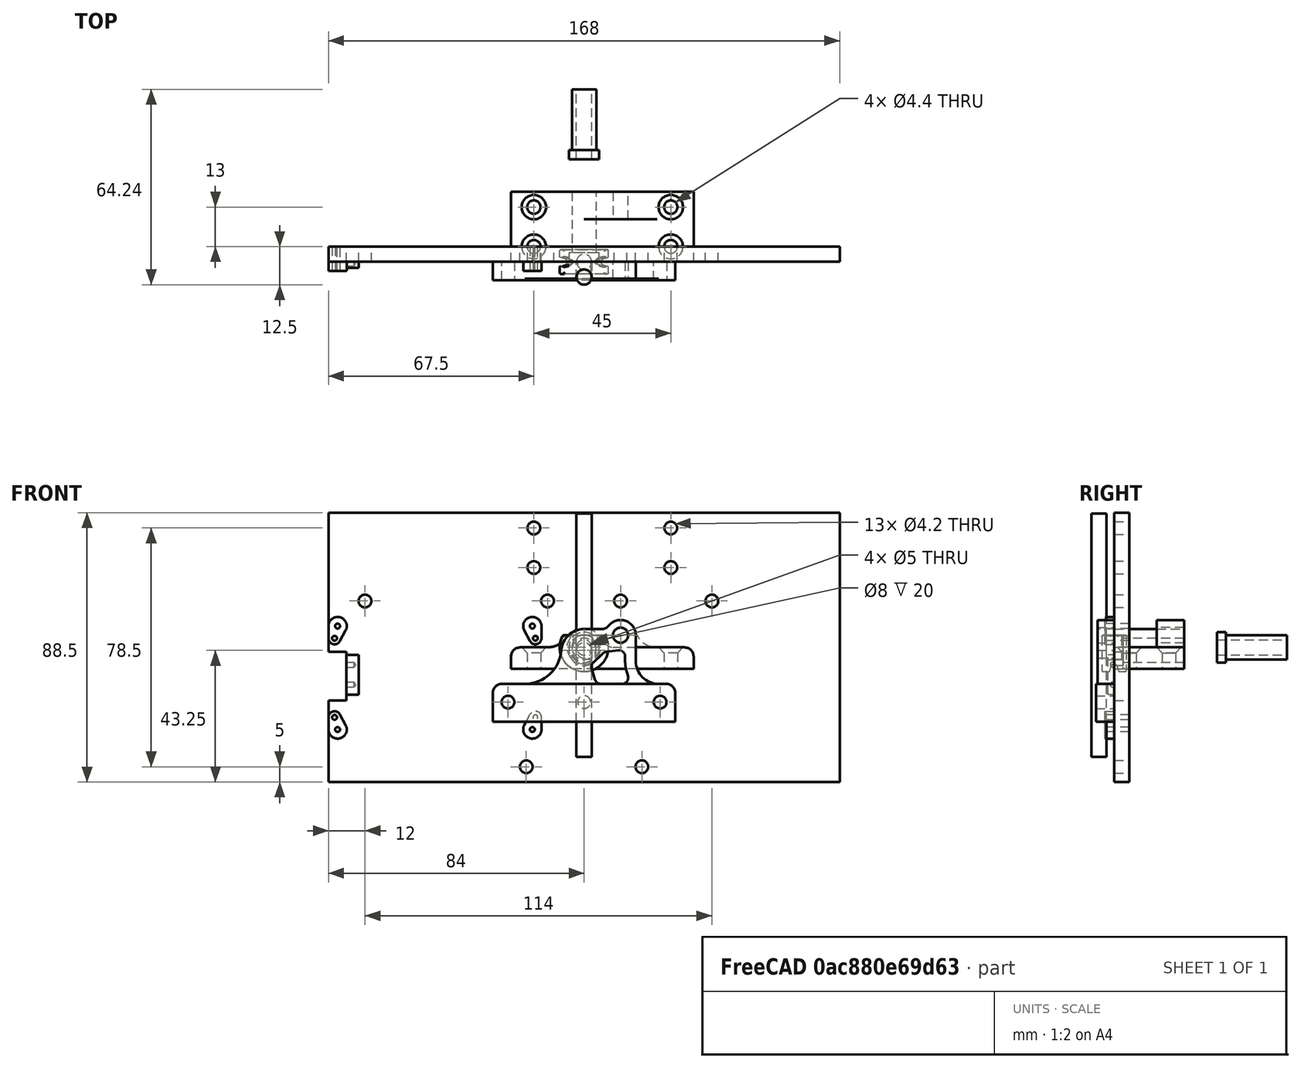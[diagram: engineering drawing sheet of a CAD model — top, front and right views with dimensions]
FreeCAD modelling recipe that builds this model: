
FCSTD DOCUMENT  (FreeCAD 0.18R14555 (Git shallow))
Label: door
License: All rights reserved
LicenseURL: http://en.wikipedia.org/wiki/All_rights_reserved
objects: Sketcher::SketchObject×18, TechDraw::DrawViewDimension×18, PartDesign::Pocket×7, PartDesign::Body×6, TechDraw::DrawProjGroupItem×5, PartDesign::Pad×4, PartDesign::Revolution×3, PartDesign::Hole×3, TechDraw::DrawSVGTemplate×3, TechDraw::DrawViewAnnotation×3, TechDraw::DrawProjGroup×3, TechDraw::DrawPage×3, PartDesign::Plane×2, PartDesign::Fillet×2, TechDraw::DrawViewSymbol×2, TechDraw::DrawViewPart×2, PartDesign::Line×1, TechDraw::DrawViewSection×1
note: 63 computed .brp shape members not serialized (recipe doc carries the construction recipe); baked Part::Feature solids carry a one-line shape summary decoded from their .brp

FEATURE [Sketcher::SketchObject] Sketch  label="Base"
  MapMode = 5
  Placement = pos=(0,0,0) rot=(1,0,0;1.5708rad)
  Support = -> [XZ_Plane]
  sketch-geometry (34):
    g0: LineSegment StartX=-84 StartY=44.25 StartZ=0 EndX=84 EndY=44.25 EndZ=0
    g1: LineSegment StartX=84 StartY=44.25 StartZ=0 EndX=84 EndY=-44.25 EndZ=0
    g2: LineSegment StartX=84 StartY=-44.25 StartZ=0 EndX=-84 EndY=-44.25 EndZ=0
    g3: LineSegment StartX=-84 StartY=-44.25 StartZ=0 EndX=-84 EndY=44.25 EndZ=0
    g4: LineSegment StartX=-4 StartY=43.25 StartZ=0 EndX=4 EndY=43.25 EndZ=0
    g5: LineSegment StartX=4 StartY=43.25 StartZ=0 EndX=4 EndY=37.25 EndZ=0
    g6: LineSegment StartX=-4 StartY=37.25 StartZ=0 EndX=-4 EndY=43.25 EndZ=0
    g7: LineSegment StartX=-2.5 StartY=54.25 StartZ=0 EndX=2.5 EndY=54.25 EndZ=0
    g8: LineSegment StartX=2.5 StartY=54.25 StartZ=0 EndX=2.5 EndY=-21.75 EndZ=0
    g9: LineSegment StartX=-4 StartY=-21.75 StartZ=0 EndX=-2.5 EndY=-21.75 EndZ=0
    g10: LineSegment StartX=4 StartY=-21.75 StartZ=0 EndX=4 EndY=-25.75 EndZ=0
    g11: LineSegment StartX=-4 StartY=-25.75 StartZ=0 EndX=-4 EndY=-21.75 EndZ=0
    g12: LineSegment StartX=-2.5 StartY=-21.75 StartZ=0 EndX=-2.5 EndY=54.25 EndZ=0
    g13: LineSegment StartX=2.5 StartY=-21.75 StartZ=0 EndX=4 EndY=-21.75 EndZ=0
    g14: LineSegment StartX=-4 StartY=-25.75 StartZ=0 EndX=4 EndY=-25.75 EndZ=0
    g15: LineSegment [constr] StartX=-40 StartY=30.25 StartZ=0 EndX=-7.5 EndY=30.25 EndZ=0
    g16: ArcOfCircle [constr] CenterX=-7.5 CenterY=27.25 CenterZ=0 NormalX=0 NormalY=0 NormalZ=1 AngleXU=0 Radius=3 StartAngle=0 EndAngle=1.5708
    g17: LineSegment [constr] StartX=-4.5 StartY=27.25 StartZ=0 EndX=-4.5 EndY=-23.75 EndZ=0
    g18: LineSegment [constr] StartX=-4.5 StartY=-23.75 StartZ=0 EndX=4.5 EndY=-23.75 EndZ=0
    g19: LineSegment [constr] StartX=4.5 StartY=-23.75 StartZ=0 EndX=4.5 EndY=27.25 EndZ=0
    g20: ArcOfCircle [constr] CenterX=7.5 CenterY=27.25 CenterZ=0 NormalX=0 NormalY=0 NormalZ=1 AngleXU=0 Radius=3 StartAngle=1.5708 EndAngle=3.14159
    g21: LineSegment [constr] StartX=7.5 StartY=30.25 StartZ=0 EndX=40 EndY=30.25 EndZ=0
    g22: LineSegment StartX=-4 StartY=51.25 StartZ=0 EndX=4 EndY=51.25 EndZ=0
    g23: LineSegment StartX=4 StartY=51.25 StartZ=0 EndX=4 EndY=45.25 EndZ=0
    g24: LineSegment StartX=4 StartY=45.25 StartZ=0 EndX=-4 EndY=45.25 EndZ=0
    g25: LineSegment StartX=-4 StartY=45.25 StartZ=0 EndX=-4 EndY=51.25 EndZ=0
    g26: Circle [constr] CenterX=7.5 CenterY=27.25 CenterZ=0 NormalX=0 NormalY=0 NormalZ=1 AngleXU=0 Radius=3
    g27: Circle [constr] CenterX=-7.5 CenterY=27.25 CenterZ=0 NormalX=0 NormalY=0 NormalZ=1 AngleXU=0 Radius=3
    g28: LineSegment StartX=5 StartY=37.25 StartZ=0 EndX=5 EndY=34.25 EndZ=0
    g29: LineSegment StartX=5 StartY=34.25 StartZ=0 EndX=-5 EndY=34.25 EndZ=0
    g30: LineSegment StartX=-5 StartY=34.25 StartZ=0 EndX=-5 EndY=37.25 EndZ=0
    g31: LineSegment StartX=5 StartY=37.25 StartZ=0 EndX=4 EndY=37.25 EndZ=0
    g32: LineSegment [constr] StartX=4 StartY=37.25 StartZ=0 EndX=-4 EndY=37.25 EndZ=0
    g33: LineSegment StartX=-5 StartY=37.25 StartZ=0 EndX=-4 EndY=37.25 EndZ=0
  constraints (89):
    c: Coincident(g0,g1)
    c: Coincident(g1,g2)
    c: Coincident(g2,g3)
    c: Coincident(g3,g0)
    c: Horizontal(g2)
    c: Vertical(g3)
    c: DistanceY(g1,g1) = 88.5  'doorHeight'
    c: DistanceX(g0,g0) = 168  'doorWidth'
    c: Symmetric(g0,g1,g-1)
    c: Symmetric(g0,g0,g-2)
    c: Coincident(g4,g5)
    c: Coincident(g6,g4)
    c: Vertical(g5)
    c: Vertical(g6)
    c: Symmetric(g4,g4,g-2)
    c: DistanceY(g4,g0) = 1
    c: DistanceY(g5,g5) = 6  'bushingLength'
    c: DistanceX(g4,g4) = 8
    c: Coincident(g7,g8)
    c: Coincident(g12,g7)
    c: Vertical(g8)
    c: Symmetric(g7,g7,g-2)
    c: DistanceX(g7,g7) = 5  'shaftOD'
    c: Coincident(g13,g10)
    c: Coincident(g11,g9)
    c: Horizontal(g9)
    c: Vertical(g10)
    c: Coincident(g9,g12)
    c: Coincident(g13,g8)
    c: Tangent(g9,g13)
    c: Equal(g13,g9)
    c: Equal(g10,g11)
    c: DistanceX(g9,g10) = 8  'springNotchOD'
    c: Coincident(g14,g11)
    c: Coincident(g14,g10)
    c: Vertical(g12)
    c: DistanceY(g11,g11) = 4  'springNotchHeight'
    c: DistanceY(g11,g7) = 80  'shaftLength'
    c: Horizontal(g15)
    c: Tangent(g15,g16) = 1.5708
    c: Tangent(g16,g17) = 1.5708
    c: Coincident(g17,g18)
    c: Coincident(g18,g19)
    c: Tangent(g19,g20) = 1.5708
    c: Tangent(g20,g21) = 1.5708
    c: PointOnObject(g15,g21)
    c: Horizontal(g21)
    c: Radius(g20) = 3  'rolerOD'
    c: Symmetric(g20,g16,g-2)
    c: Equal(g15,g21)
    c: Symmetric(g11,g9,g18)
    c: Coincident(g22,g23)
    c: Coincident(g23,g24)
    c: Coincident(g24,g25)
    c: Coincident(g25,g22)
    c: Horizontal(g24)
    c: Vertical(g23)
    c: Vertical(g25)
    c: Symmetric(g22,g22,g-2)
    c: Equal(g23,g5)
    c: Equal(g24,g4)
    c: Symmetric(g17,g18,g-2)
    c: DistanceX(g10,g18) = 0.5
    c: DistanceY(g0,g23) = 1
    c: DistanceX(g16,g20) = 15  'rolerDist'
    c: Coincident(g26,g20)
    c: PointOnObject(g20,g26)
    c: Coincident(g27,g16)
    c: PointOnObject(g15,g27)
    c: DistanceX(g15,g21) = 80
    c: DistanceY(g15,g0) = 14  'rolerHeight'
    c: DistanceY(g11,g0) = 70
    c: Coincident(g28,g29)
    c: Coincident(g29,g30)
    c: Horizontal(g29)
    c: Vertical(g28)
    c: Vertical(g30)
    c: Coincident(g31,g28)
    c: Horizontal(g31)
    c: Coincident(g31,g5)
    c: Coincident(g32,g5)
    c: Horizontal(g32)
    c: Coincident(g32,g6)
    c: Coincident(g33,g30)
    c: Horizontal(g33)
    c: Coincident(g33,g6)
    c: Equal(g33,g31)
    c: DistanceX(g29,g29) = 10
    c: DistanceY(g30,g30) = 3
FEATURE [Sketcher::SketchObject] Sketch001
  MapMode = 5
  Placement = pos=(0,0,0) rot=(1,0,0;1.5708rad)
  Support = -> [XZ_Plane]
  expr: Constraints[7] = Sketch.Constraints.doorWidth
  expr: Constraints[6] = Sketch.Constraints.doorHeight
  sketch-geometry (8):
    g0: LineSegment [constr] StartX=-84 StartY=44.25 StartZ=0 EndX=84 EndY=44.25 EndZ=0
    g1: LineSegment [constr] StartX=84 StartY=44.25 StartZ=0 EndX=84 EndY=-44.25 EndZ=0
    g2: LineSegment [constr] StartX=84 StartY=-44.25 StartZ=0 EndX=-84 EndY=-44.25 EndZ=0
    g3: LineSegment [constr] StartX=-84 StartY=-44.25 StartZ=0 EndX=-84 EndY=44.25 EndZ=0
    g4: LineSegment StartX=-84 StartY=44.25 StartZ=0 EndX=84 EndY=44.25 EndZ=0
    g5: LineSegment StartX=84 StartY=44.25 StartZ=0 EndX=84 EndY=-44.25 EndZ=0
    g6: LineSegment StartX=84 StartY=-44.25 StartZ=0 EndX=-84 EndY=-44.25 EndZ=0
    g7: LineSegment StartX=-84 StartY=-44.25 StartZ=0 EndX=-84 EndY=44.25 EndZ=0
  constraints (19):
    c: Coincident(g0,g1)
    c: Coincident(g1,g2)
    c: Coincident(g2,g3)
    c: Coincident(g3,g0)
    c: Horizontal(g2)
    c: Vertical(g3)
    c: DistanceY(g1,g1) = 88.5
    c: DistanceX(g0,g0) = 168
    c: Symmetric(g0,g1,g-1)
    c: Symmetric(g0,g0,g-2)
    c: Coincident(g4,g5)
    c: Coincident(g5,g6)
    c: Coincident(g6,g7)
    c: Coincident(g7,g4)
    c: Horizontal(g4)
    c: Vertical(g5)
    c: Coincident(g4,g0)
    c: Coincident(g6,g2)
    c: Coincident(g1,g5)
FEATURE [PartDesign::Pad] Pad
  Length = 5
  Length2 = 100
  Placement = pos=(0,0,0) rot=(1,0,0;1.5708rad)
  Profile = -> Sketch001
  Reversed = true
  Type = 0
FEATURE [Sketcher::SketchObject] Sketch013  label="BushingSketch"
  MapMode = 5
  Support = -> [XY_Plane003]
  sketch-geometry (6):
    g0: LineSegment StartX=2.5 StartY=56.7373 StartZ=0 EndX=4 EndY=56.7373 EndZ=0
    g1: LineSegment StartX=4 StartY=56.7373 StartZ=0 EndX=4 EndY=36.7373 EndZ=0
    g2: LineSegment StartX=4 StartY=36.7373 StartZ=0 EndX=5 EndY=36.7373 EndZ=0
    g3: LineSegment StartX=5 StartY=36.7373 StartZ=0 EndX=5 EndY=33.7373 EndZ=0
    g4: LineSegment StartX=5 StartY=33.7373 StartZ=0 EndX=2.5 EndY=33.7373 EndZ=0
    g5: LineSegment StartX=2.5 StartY=33.7373 StartZ=0 EndX=2.5 EndY=56.7373 EndZ=0
  constraints (17):
    c: Horizontal(g0)
    c: Coincident(g0,g1)
    c: Vertical(g1)
    c: Coincident(g1,g2)
    c: Horizontal(g2)
    c: Coincident(g2,g3)
    c: Vertical(g3)
    c: Coincident(g3,g4)
    c: Horizontal(g4)
    c: Coincident(g4,g5)
    c: Coincident(g5,g0)
    c: Vertical(g5)
    c: DistanceX(g-1,g0) = 4
    c: DistanceX(g-1,g3) = 5
    c: DistanceX(g-1,g4) = 2.5
    c: DistanceY(g3,g3) = 3
    c: DistanceY(g3,g0) = 23  'BushingHeight'
FEATURE [PartDesign::Revolution] Revolution001
  Angle = 360
  Axis = (0,1,0)
  Base = (0,0,0)
  Profile = -> Sketch013
  ReferenceAxis = -> Sketch013 [V_Axis]
  Reversed = true
FEATURE [PartDesign::Body] Body003  label="Bushing"
  Group = -> [Sketch013,Revolution001]
  Origin = -> Origin003
  Tip = -> Revolution001
FEATURE [Sketcher::SketchObject] Sketch014
  MapMode = 5
  Placement = pos=(0,0,0) rot=(0.57735,0.57735,0.57735;2.0944rad)
  Support = -> [YZ_Plane004]
  sketch-geometry (11):
    g0: LineSegment StartX=-4 StartY=0 StartZ=0 EndX=-4 EndY=-8 EndZ=0
    g1: LineSegment StartX=-4 StartY=-8 StartZ=0 EndX=-1.5 EndY=-8 EndZ=0
    g2: LineSegment StartX=-1.5 StartY=-8 StartZ=0 EndX=-0.956943 EndY=-6.20972 EndZ=0
    g3: ArcOfCircle CenterX=2e-16 CenterY=-6.5 CenterZ=0 NormalX=0 NormalY=0 NormalZ=1 AngleXU=0 Radius=1 StartAngle=0.294515 EndAngle=2.84708
    g4: LineSegment StartX=0.956943 StartY=-6.20972 StartZ=0 EndX=1.5 EndY=-8 EndZ=0
    g5: LineSegment StartX=1.5 StartY=-8 StartZ=0 EndX=4 EndY=-8 EndZ=0
    g6: LineSegment StartX=4 StartY=-8 StartZ=0 EndX=4 EndY=0 EndZ=0
    g7: LineSegment StartX=4 StartY=0 StartZ=0 EndX=-4 EndY=0 EndZ=0
    g8: LineSegment [constr] StartX=-1.5 StartY=-8 StartZ=0 EndX=2e-16 EndY=-8 EndZ=0
    g9: LineSegment [constr] StartX=2e-16 StartY=-8 StartZ=0 EndX=1.5 EndY=-8 EndZ=0
    g10: LineSegment [constr] StartX=2e-16 StartY=-8 StartZ=0 EndX=2e-16 EndY=-6.5 EndZ=0
  constraints (29):
    c: PointOnObject(g0,g-1)
    c: Vertical(g0)
    c: Coincident(g0,g1)
    c: Horizontal(g1)
    c: Coincident(g1,g2)
    c: Tangent(g2,g3) = 1.5708
    c: Tangent(g3,g4) = 1.5708
    c: Coincident(g4,g5)
    c: Horizontal(g5)
    c: Coincident(g5,g6)
    c: Vertical(g6)
    c: Coincident(g6,g7)
    c: Coincident(g7,g0)
    c: PointOnObject(g4,g1)
    c: Equal(g1,g5)
    c: Coincident(g8,g1)
    c: Horizontal(g8)
    c: Coincident(g9,g8)
    c: Coincident(g9,g4)
    c: Equal(g8,g9)
    c: Coincident(g10,g8)
    c: Vertical(g10)
    c: Coincident(g3,g10)
    c: DistanceY(g0,g0) = 8
    c: DistanceX(g7,g7) = 8
    c: DistanceX(g1,g4) = 3
    c: DistanceY(g10,g10) = 1.5
    c: Radius(g3) = 1
    c: Symmetric(g6,g0,g-2)
FEATURE [PartDesign::Revolution] Revolution002
  Angle = 360
  Axis = (1e-16,1,-1e-16)
  Base = (0,0,0)
  Placement = pos=(0,0,0) rot=(0.57735,0.57735,0.57735;2.0944rad)
  Profile = -> Sketch014
  ReferenceAxis = -> Y_Axis004
FEATURE [PartDesign::Plane] DatumPlane003
  AttachmentOffset = pos=(0,0,4) rot=(0,0,1;0rad)
  Length = 24
  MapMode = 5
  Placement = pos=(0,0,4) rot=(0,0,1;0rad)
  ResizeMode = 0
  Support = -> [XY_Plane004]
  Width = 24
FEATURE [Sketcher::SketchObject] Sketch015
  MapMode = 5
  Placement = pos=(0,0,0) rot=(1,0,0;1.5708rad)
  Support = -> [XZ_Plane004]
  sketch-geometry (4):
    g0: LineSegment StartX=-8 StartY=20 StartZ=0 EndX=8 EndY=20 EndZ=0
    g1: LineSegment StartX=8 StartY=20 StartZ=0 EndX=8 EndY=4 EndZ=0
    g2: LineSegment StartX=8 StartY=4 StartZ=0 EndX=-8 EndY=4 EndZ=0
    g3: LineSegment StartX=-8 StartY=4 StartZ=0 EndX=-8 EndY=20 EndZ=0
  constraints (11):
    c: Coincident(g0,g1)
    c: Coincident(g1,g2)
    c: Coincident(g2,g3)
    c: Coincident(g3,g0)
    c: Horizontal(g2)
    c: Vertical(g1)
    c: Vertical(g3)
    c: Symmetric(g0,g0,g-2)
    c: DistanceX(g0,g0) = 16
    c: Equal(g0,g1)
    c: DistanceY(g-1,g1) = 4
FEATURE [PartDesign::Pocket] Pocket
  BaseFeature = -> Revolution002
  Length = 5
  Length2 = 100
  Midplane = true
  Placement = pos=(0,0,0) rot=(0.57735,0.57735,0.57735;2.0944rad)
  Profile = -> Sketch015
  Type = 1
FEATURE [Sketcher::SketchObject] Sketch016
  MapMode = 5
  Placement = pos=(0,0,4) rot=(0,0,1;0rad)
  Support = -> [DatumPlane003]
  expr: Constraints[1] = <<Base>>.Constraints.shaftOD
  sketch-geometry (1):
    g0: Circle CenterX=0 CenterY=0 CenterZ=0 NormalX=0 NormalY=0 NormalZ=1 AngleXU=0 Radius=2.5
  constraints (2):
    c: Coincident(g0,g-1)
    c: Diameter(g0) = 5
FEATURE [PartDesign::Pocket] Pocket002
  BaseFeature = -> Pocket
  Length = 8
  Length2 = 100
  Placement = pos=(0,0,0) rot=(0.57735,0.57735,0.57735;2.0944rad)
  Profile = -> Sketch016
  Type = 0
FEATURE [PartDesign::Fillet] Fillet
  Base = -> Pocket002 [Edge3,Edge18,Edge25,Edge28]
  BaseFeature = -> Pocket002
  Placement = pos=(0,0,0) rot=(0.57735,0.57735,0.57735;2.0944rad)
  Radius = 0.4
FEATURE [PartDesign::Fillet] Fillet001
  Base = -> Fillet [Edge1]
  BaseFeature = -> Fillet
  Placement = pos=(0,0,0) rot=(0.57735,0.57735,0.57735;2.0944rad)
  Radius = 0.4
FEATURE [PartDesign::Body] Body004  label="Slider"
  Group = -> [Sketch014,Revolution002,DatumPlane003,Sketch015,Pocket,Sketch016,Pocket002,Fillet,Fillet001]
  Origin = -> Origin004
  Tip = -> Fillet001
FEATURE [PartDesign::Line] DatumLine
  AttacherType = Attacher::AttachEngineLine
  AttachmentOffset = pos=(0,5,0) rot=(0,0,1;0rad)
  MapMode = 17
  Placement = pos=(0,-5,-1.1e-15) rot=(1,0,0;3.14159rad)
  Support = -> [XZ_Plane001]
FEATURE [PartDesign::Plane] DatumPlane
  AttachmentOffset = pos=(0,0,5) rot=(0,0,1;0rad)
  Length = 28
  MapMode = 5
  Placement = pos=(0,-5,-1.1e-15) rot=(1,0,0;1.5708rad)
  ResizeMode = 0
  Support = -> [XZ_Plane001]
  Width = 88
FEATURE [Sketcher::SketchObject] Sketch004
  MapMode = 5
  Placement = pos=(0,-5,-1.1e-15) rot=(1,0,0;1.5708rad)
  Support = -> [DatumPlane]
  expr: Constraints[9] = Sketch.Constraints.shaftOD / 2
  expr: Constraints[8] = Sketch.Constraints.shaftLength
  sketch-geometry (4):
    g0: LineSegment StartX=0 StartY=-36.0556 StartZ=0 EndX=2.5 EndY=-36.0556 EndZ=0
    g1: LineSegment StartX=2.5 StartY=-36.0556 StartZ=0 EndX=2.5 EndY=43.9444 EndZ=0
    g2: LineSegment StartX=2.5 StartY=43.9444 StartZ=0 EndX=0 EndY=43.9444 EndZ=0
    g3: LineSegment StartX=0 StartY=43.9444 StartZ=0 EndX=0 EndY=-36.0556 EndZ=0
  constraints (11):
    c: Horizontal(g0)
    c: Vertical(g1)
    c: Coincident(g1,g2)
    c: Coincident(g2,g3)
    c: Vertical(g3)
    c: Coincident(g0,g3)
    c: Horizontal(g2)
    c: PointOnObject(g2,g-2)
    c: DistanceY(g3,g3) = 80
    c: DistanceX(g2,g2) = 2.5
    c: Coincident(g0,g1)
FEATURE [PartDesign::Revolution] Revolution
  Angle = 360
  Axis = (0,-2e-16,1)
  Base = (0,-5,-1.1e-15)
  Placement = pos=(0,-5,-1e-15) rot=(1,0,0;1.5708rad)
  Profile = -> Sketch004
  ReferenceAxis = -> Sketch004 [V_Axis]
  Reversed = true
FEATURE [PartDesign::Body] Body001  label="Pin"
  Group = -> [DatumLine,DatumPlane,Sketch004,Revolution]
  Origin = -> Origin001
  Tip = -> Revolution
FEATURE [Sketcher::SketchObject] Sketch018
  MapMode = 5
  Placement = pos=(0,0,0) rot=(1,0,0;1.5708rad)
  Support = -> [XZ_Plane]
  expr: Constraints[10] = <<Base>>.Constraints.doorWidth / 2mm
  sketch-geometry (46):
    g0: LineSegment [constr] StartX=-84 StartY=10 StartZ=0 EndX=-14 EndY=10 EndZ=0
    g1: LineSegment [constr] StartX=-14 StartY=10 StartZ=0 EndX=-14 EndY=-30 EndZ=0
    g2: LineSegment [constr] StartX=-14 StartY=-30 StartZ=0 EndX=-84 EndY=-30 EndZ=0
    g3: LineSegment [constr] StartX=-84 StartY=-30 StartZ=0 EndX=-84 EndY=10 EndZ=0
    g4: LineSegment [constr] StartX=-81 StartY=7 StartZ=0 EndX=-17 EndY=7 EndZ=0
    g5: LineSegment [constr] StartX=-17 StartY=7 StartZ=0 EndX=-17 EndY=-27 EndZ=0
    g6: LineSegment [constr] StartX=-17 StartY=-27 StartZ=0 EndX=-81 EndY=-27 EndZ=0
    g7: LineSegment [constr] StartX=-81 StartY=-27 StartZ=0 EndX=-81 EndY=7 EndZ=0
    g8: Circle [constr] CenterX=-81 CenterY=7 CenterZ=0 NormalX=0 NormalY=0 NormalZ=1 AngleXU=0 Radius=0.8
    g9: Circle [constr] CenterX=-17 CenterY=7 CenterZ=0 NormalX=0 NormalY=0 NormalZ=1 AngleXU=0 Radius=0.8
    g10: Circle [constr] CenterX=-17 CenterY=-27 CenterZ=0 NormalX=0 NormalY=0 NormalZ=1 AngleXU=0 Radius=0.8
    g11: Circle [constr] CenterX=-81 CenterY=-27 CenterZ=0 NormalX=0 NormalY=0 NormalZ=1 AngleXU=0 Radius=0.8
    g12: LineSegment [constr] StartX=-84 StartY=-2.5 StartZ=0 EndX=-78.1 EndY=-2.5 EndZ=0
    g13: LineSegment [constr] StartX=-78.1 StartY=-2.5 StartZ=0 EndX=-78.1 EndY=-15.5 EndZ=0
    g14: LineSegment [constr] StartX=-78.1 StartY=-15.5 StartZ=0 EndX=-84 EndY=-15.5 EndZ=0
    g15: LineSegment [constr] StartX=-84 StartY=-15.5 StartZ=0 EndX=-84 EndY=-2.5 EndZ=0
    g16: Circle [constr] CenterX=-17 CenterY=7 CenterZ=0 NormalX=0 NormalY=0 NormalZ=1 AngleXU=0 Radius=3
    g17: Circle [constr] CenterX=-81 CenterY=7 CenterZ=0 NormalX=0 NormalY=0 NormalZ=1 AngleXU=0 Radius=3
    g18: Circle [constr] CenterX=-81 CenterY=-27 CenterZ=0 NormalX=0 NormalY=0 NormalZ=1 AngleXU=0 Radius=3
    g19: Circle [constr] CenterX=-17 CenterY=-27 CenterZ=0 NormalX=0 NormalY=0 NormalZ=1 AngleXU=0 Radius=3
    g20: LineSegment StartX=-78.1 StartY=-2.5 StartZ=0 EndX=-74.1 EndY=-2.5 EndZ=0
    g21: LineSegment StartX=-74.1 StartY=-2.5 StartZ=0 EndX=-74.1 EndY=-15.5 EndZ=0
    g22: LineSegment StartX=-74.1 StartY=-15.5 StartZ=0 EndX=-78.1 EndY=-15.5 EndZ=0
    g23: LineSegment StartX=-78.1 StartY=-15.5 StartZ=0 EndX=-78.1 EndY=-2.5 EndZ=0
    g24: LineSegment [constr] StartX=-49 StartY=7 StartZ=0 EndX=-49 EndY=-27 EndZ=0
    g25: LineSegment [constr] StartX=-82 StartY=3 StartZ=0 EndX=-16 EndY=3 EndZ=0
    g26: LineSegment [constr] StartX=-16 StartY=3 StartZ=0 EndX=-16 EndY=-23 EndZ=0
    g27: LineSegment [constr] StartX=-16 StartY=-23 StartZ=0 EndX=-82 EndY=-23 EndZ=0
    g28: LineSegment [constr] StartX=-82 StartY=-23 StartZ=0 EndX=-82 EndY=3 EndZ=0
    g29: LineSegment [constr] StartX=-17 StartY=-10 StartZ=0 EndX=-81 EndY=-10 EndZ=0
    g30: ArcOfCircle CenterX=-17 CenterY=7 CenterZ=0 NormalX=0 NormalY=0 NormalZ=1 AngleXU=0 Radius=3 StartAngle=2e-16 EndAngle=3.63155
    g31: ArcOfCircle CenterX=-16 CenterY=3 CenterZ=0 NormalX=0 NormalY=0 NormalZ=1 AngleXU=0 Radius=2 StartAngle=3.63155 EndAngle=6.28319
    g32: LineSegment StartX=-19.6471 StartY=5.58824 StartZ=0 EndX=-17.7647 EndY=2.05882 EndZ=0
    g33: LineSegment StartX=-14 StartY=7 StartZ=0 EndX=-14 EndY=3 EndZ=0
    g34: ArcOfCircle CenterX=-17 CenterY=-27 CenterZ=0 NormalX=0 NormalY=0 NormalZ=1 AngleXU=0 Radius=3 StartAngle=2.65164 EndAngle=6.28319
    g35: ArcOfCircle CenterX=-16 CenterY=-23 CenterZ=0 NormalX=0 NormalY=0 NormalZ=1 AngleXU=0 Radius=2 StartAngle=1e-16 EndAngle=2.65164
    g36: LineSegment StartX=-14 StartY=-27 StartZ=0 EndX=-14 EndY=-23 EndZ=0
    g37: LineSegment StartX=-19.6471 StartY=-25.5882 StartZ=0 EndX=-17.7647 EndY=-22.0588 EndZ=0
    g38: ArcOfCircle CenterX=-82 CenterY=-23 CenterZ=0 NormalX=0 NormalY=0 NormalZ=1 AngleXU=0 Radius=2 StartAngle=0.489957 EndAngle=3.14159
    g39: ArcOfCircle CenterX=-81 CenterY=-27 CenterZ=0 NormalX=0 NormalY=0 NormalZ=1 AngleXU=0 Radius=3 StartAngle=3.14159 EndAngle=6.77314
    g40: LineSegment StartX=-84 StartY=-23 StartZ=0 EndX=-84 EndY=-27 EndZ=0
    g41: LineSegment StartX=-80.2353 StartY=-22.0588 StartZ=0 EndX=-78.3529 EndY=-25.5882 EndZ=0
    g42: ArcOfCircle CenterX=-81 CenterY=7 CenterZ=0 NormalX=0 NormalY=0 NormalZ=1 AngleXU=0 Radius=3 StartAngle=5.79323 EndAngle=9.42478
    g43: ArcOfCircle CenterX=-82 CenterY=3 CenterZ=0 NormalX=0 NormalY=0 NormalZ=1 AngleXU=0 Radius=2 StartAngle=3.14159 EndAngle=5.79323
    g44: LineSegment StartX=-84 StartY=7 StartZ=0 EndX=-84 EndY=3 EndZ=0
    g45: LineSegment StartX=-78.3529 StartY=5.58824 StartZ=0 EndX=-80.2353 EndY=2.05882 EndZ=0
  constraints (110):
    c: Coincident(g0,g1)
    c: Coincident(g1,g2)
    c: Coincident(g2,g3)
    c: Coincident(g3,g0)
    c: Horizontal(g0)
    c: Horizontal(g2)
    c: Vertical(g1)
    c: Vertical(g3)
    c: DistanceX(g2,g2) = 70
    c: DistanceY(g1,g1) = 40
    c: DistanceX(g0,g-1) = 84
    c: DistanceY(g-1,g0) = 10
    c: Coincident(g4,g5)
    c: Coincident(g5,g6)
    c: Coincident(g6,g7)
    c: Coincident(g7,g4)
    c: Horizontal(g4)
    c: Horizontal(g6)
    c: Vertical(g5)
    c: Vertical(g7)
    c: DistanceX(g4,g0) = 3
    c: DistanceY(g4,g0) = 3
    c: DistanceX(g0,g4) = 3
    c: DistanceY(g2,g6) = 3
    c: Coincident(g8,g4)
    c: Coincident(g9,g4)
    c: Coincident(g10,g5)
    c: Coincident(g11,g6)
    c: Diameter(g11) = 1.6
    c: Equal(g11,g8)
    c: Equal(g11,g9)
    c: Equal(g11,g10)
    c: Coincident(g12,g13)
    c: Coincident(g13,g14)
    c: Coincident(g14,g15)
    c: Coincident(g15,g12)
    c: Horizontal(g12)
    c: Horizontal(g14)
    c: Vertical(g13)
    c: Vertical(g15)
    c: PointOnObject(g12,g3)
    c: DistanceX(g14,g13) = 5.9
    c: DistanceY(g2,g13) = 14.5
    c: DistanceY(g13,g13) = 13
    c: Coincident(g16,g4)
    c: Coincident(g17,g4)
    c: Coincident(g18,g6)
    c: Coincident(g19,g5)
    c: Coincident(g20,g21)
    c: Coincident(g21,g22)
    c: Coincident(g22,g23)
    c: Coincident(g23,g20)
    c: Horizontal(g20)
    c: Horizontal(g22)
    c: Vertical(g21)
    c: Coincident(g20,g12)
    c: Coincident(g22,g13)
    c: DistanceX(g20,g20) = 4
    c: Diameter(g17) = 6
    c: Equal(g17,g16)
    c: Equal(g17,g19)
    c: Equal(g17,g18)
    c: PointOnObject(g24,g4)
    c: PointOnObject(g24,g6)
    c: Symmetric(g17,g16,g24)
    c: Coincident(g25,g26)
    c: Coincident(g26,g27)
    c: Coincident(g27,g28)
    c: Coincident(g28,g25)
    c: Horizontal(g27)
    c: Vertical(g28)
    c: Symmetric(g25,g25,g24)
    c: DistanceX(g25,g25) = 66
    c: PointOnObject(g29,g5)
    c: PointOnObject(g29,g7)
    c: Symmetric(g19,g16,g29)
    c: Symmetric(g26,g25,g29)
    c: DistanceY(g26,g26) = 26
    c: Tangent(g30,g33) = 1.5708
    c: Tangent(g30,g32) = -1.5708
    c: Tangent(g32,g31) = -1.5708
    c: Tangent(g33,g31) = 1.5708
    c: Coincident(g30,g16)
    c: Equal(g30,g16)
    c: Coincident(g31,g25)
    c: Vertical(g33)
    c: Tangent(g34,g37) = 1.5708
    c: Tangent(g34,g36) = -1.5708
    c: Tangent(g36,g35) = -1.5708
    c: Tangent(g37,g35) = 1.5708
    c: Vertical(g36)
    c: Coincident(g34,g5)
    c: Equal(g34,g19)
    c: Coincident(g35,g26)
    c: Tangent(g38,g41) = 1.5708
    c: Tangent(g38,g40) = -1.5708
    c: Tangent(g40,g39) = -1.5708
    c: Tangent(g41,g39) = 1.5708
    c: Vertical(g40)
    c: Coincident(g38,g27)
    c: Coincident(g39,g6)
    c: Equal(g39,g18)
    c: Tangent(g42,g45) = 1.5708
    c: Tangent(g42,g44) = -1.5708
    c: Tangent(g44,g43) = -1.5708
    c: Tangent(g45,g43) = 1.5708
    c: Vertical(g44)
    c: Coincident(g42,g17)
    c: Equal(g42,g17)
    c: Coincident(g43,g25)
FEATURE [Sketcher::SketchObject] Sketch020  label="lockSketch"
  MapMode = 5
  Placement = pos=(0,0,0) rot=(1,0,0;1.5708rad)
  Support = -> [XZ_Plane007]
  sketch-geometry (35):
    g0: Circle CenterX=0 CenterY=-1 CenterZ=0 NormalX=0 NormalY=0 NormalZ=1 AngleXU=0 Radius=2.5
    g1: LineSegment StartX=30 StartY=-24.5 StartZ=0 EndX=-30 EndY=-24.5 EndZ=0
    g2: LineSegment [constr] StartX=25 StartY=-18 StartZ=0 EndX=0 EndY=-18 EndZ=0
    g3: LineSegment [constr] StartX=0 StartY=-18 StartZ=0 EndX=-25 EndY=-18 EndZ=0
    g4: Circle CenterX=-25 CenterY=-18 CenterZ=0 NormalX=0 NormalY=0 NormalZ=1 AngleXU=0 Radius=2.1
    g5: Circle CenterX=0 CenterY=-18 CenterZ=0 NormalX=0 NormalY=0 NormalZ=1 AngleXU=0 Radius=2.1
    g6: Circle CenterX=25 CenterY=-18 CenterZ=0 NormalX=0 NormalY=0 NormalZ=1 AngleXU=0 Radius=2.1
    g7: LineSegment StartX=-27 StartY=-12 StartZ=0 EndX=-19.4422 EndY=-12 EndZ=0
    g8: Circle CenterX=12 CenterY=4 CenterZ=0 NormalX=0 NormalY=0 NormalZ=1 AngleXU=0 Radius=2.5
    g9: LineSegment StartX=-30 StartY=-24.5 StartZ=0 EndX=-30 EndY=-15 EndZ=0
    g10: ArcOfCircle CenterX=-27 CenterY=-15 CenterZ=0 NormalX=0 NormalY=0 NormalZ=1 AngleXU=0 Radius=3 StartAngle=1.5708 EndAngle=3.14159
    g11: LineSegment StartX=30 StartY=-24.5 StartZ=0 EndX=30 EndY=-15 EndZ=0
    g12: ArcOfCircle CenterX=27 CenterY=-15 CenterZ=0 NormalX=0 NormalY=0 NormalZ=1 AngleXU=0 Radius=3 StartAngle=0 EndAngle=1.5708
    g13: LineSegment StartX=27 StartY=-12 StartZ=0 EndX=24.5 EndY=-12 EndZ=0
    g14: ArcOfCircle CenterX=24.5 CenterY=-4.5 CenterZ=0 NormalX=0 NormalY=0 NormalZ=1 AngleXU=0 Radius=7.5 StartAngle=3.14159 EndAngle=4.71239
    g15: LineSegment StartX=17 StartY=-4.5 StartZ=0 EndX=17 EndY=4 EndZ=0
    g16: ArcOfCircle CenterX=12 CenterY=4 CenterZ=0 NormalX=0 NormalY=0 NormalZ=1 AngleXU=0 Radius=5 StartAngle=0 EndAngle=2.46646
    g17: ArcOfCircle CenterX=5.755 CenterY=9 CenterZ=0 NormalX=0 NormalY=0 NormalZ=1 AngleXU=0 Radius=3 StartAngle=4.71239 EndAngle=5.60805
    g18: LineSegment StartX=5.755 StartY=6 StartZ=0 EndX=9e-16 EndY=6 EndZ=0
    g19: ArcOfCircle CenterX=0 CenterY=-1.5 CenterZ=0 NormalX=0 NormalY=0 NormalZ=1 AngleXU=0 Radius=7.5 StartAngle=1.5708 EndAngle=3.06459
    g20: ArcOfCircle CenterX=-19.4422 CenterY=2e-16 CenterZ=0 NormalX=0 NormalY=0 NormalZ=1 AngleXU=0 Radius=12 StartAngle=4.71239 EndAngle=6.20619
    g21: Circle [constr] CenterX=0 CenterY=-1 CenterZ=0 NormalX=0 NormalY=0 NormalZ=1 AngleXU=0 Radius=5
    g22: Circle [constr] CenterX=12 CenterY=4 CenterZ=0 NormalX=0 NormalY=0 NormalZ=1 AngleXU=0 Radius=5
    g23: LineSegment StartX=12.5 StartY=-12 StartZ=0 EndX=5.5 EndY=-12 EndZ=0
    g24: LineSegment StartX=3.5847 StartY=-10.5759 StartZ=0 EndX=2.50952 EndY=-7 EndZ=0
    g25: LineSegment StartX=3.04281 StartY=-4.97841 StartZ=0 EndX=6.11799 EndY=-2.03871 EndZ=0
    g26: LineSegment StartX=7.25081 StartY=-1.5 StartZ=0 EndX=11.2508 EndY=-0.997705 EndZ=0
    g27: LineSegment StartX=13.5 StartY=-2.98212 StartZ=0 EndX=13.5 EndY=-4.5 EndZ=0
    g28: LineSegment StartX=13.8565 StartY=-7.27791 StartZ=0 EndX=14.4352 EndY=-9.49493 EndZ=0
    g29: ArcOfCircle CenterX=12.5 CenterY=-10 CenterZ=0 NormalX=0 NormalY=0 NormalZ=1 AngleXU=0 Radius=2 StartAngle=4.71239 EndAngle=6.53849
    g30: ArcOfCircle CenterX=5.5 CenterY=-10 CenterZ=0 NormalX=0 NormalY=0 NormalZ=1 AngleXU=0 Radius=2 StartAngle=3.43367 EndAngle=4.71239
    g31: ArcOfCircle CenterX=4.42481 CenterY=-6.42411 CenterZ=0 NormalX=0 NormalY=0 NormalZ=1 AngleXU=0 Radius=2 StartAngle=2.33367 EndAngle=3.43367
    g32: ArcOfCircle CenterX=7.5 CenterY=-3.48442 CenterZ=0 NormalX=0 NormalY=0 NormalZ=1 AngleXU=0 Radius=2 StartAngle=1.69572 EndAngle=2.33367
    g33: ArcOfCircle CenterX=11.5 CenterY=-2.98212 CenterZ=0 NormalX=0 NormalY=0 NormalZ=1 AngleXU=0 Radius=2 StartAngle=0 EndAngle=1.69572
    g34: ArcOfCircle CenterX=24.5 CenterY=-4.5 CenterZ=0 NormalX=0 NormalY=0 NormalZ=1 AngleXU=0 Radius=11 StartAngle=3.14159 EndAngle=3.39689
  constraints (87):
    c: PointOnObject(g0,g-2)
    c: DistanceY(g0,g-1) = 1
    c: Diameter(g0) = 5
    c: PointOnObject(g2,g-2)
    c: Horizontal(g2)
    c: Coincident(g2,g3)
    c: Horizontal(g3)
    c: Coincident(g4,g3)
    c: Coincident(g5,g2)
    c: Coincident(g6,g2)
    c: Equal(g2,g3)
    c: Horizontal(g7)
    c: DistanceY(g7,g0) = 11  'lockFromEdge'
    c: DistanceY(g4,g7) = 6
    c: DistanceX(g4,g6) = 50
    c: Diameter(g4) = 4.2
    c: Equal(g4,g5)
    c: Equal(g4,g6)
    c: DistanceY(g1,g7) = 12.5  'lockWidth'
    c: DistanceX(g1,g1) = 60  'lockLength'
    c: Equal(g8,g0)
    c: DistanceX(g-1,g8) = 12
    c: DistanceY(g0,g8) = 5
    c: Coincident(g1,g9)
    c: Vertical(g9)
    c: Tangent(g9,g10) = 1.5708
    c: Tangent(g10,g7) = 1.5708
    c: Symmetric(g1,g1,g-2)
    c: Radius(g10) = 3
    c: Coincident(g1,g11)
    c: Vertical(g11)
    c: Tangent(g11,g12) = -1.5708
    c: Tangent(g12,g13) = -1.5708
    c: Tangent(g13,g14) = 1.5708
    c: Tangent(g14,g15) = 1.5708
    c: Tangent(g15,g16) = -1.5708
    c: Tangent(g16,g17) = 1.5708
    c: PointOnObject(g18,g-2)
    c: Tangent(g18,g19) = -1.5708
    c: Tangent(g19,g20) = 1.5708
    c: Tangent(g20,g7) = -1.5708
    c: Horizontal(g18)
    c: DistanceY(g0,g18) = 7
    c: Radius(g19) = 7.5
    c: Radius(g20) = 12
    c: Tangent(g17,g18) = 1.5708
    c: Coincident(g16,g8)
    c: Vertical(g15)
    c: Radius(g16) = 5
    c: Radius(g17) = 3
    c: Horizontal(g13)
    c: PointOnObject(g13,g7)
    c: Radius(g14) = 7.5
    c: Equal(g12,g10)
    c: Coincident(g21,g0)
    c: Diameter(g21) = 10
    c: Coincident(g22,g8)
    c: Diameter(g22) = 10
    c: Horizontal(g23)
    c: Vertical(g27)
    c: Tangent(g28,g29) = 1.5708
    c: Tangent(g23,g29) = 1.5708
    c: Tangent(g23,g30) = 1.5708
    c: Tangent(g24,g30) = 1.5708
    c: Tangent(g24,g31) = 1.5708
    c: Tangent(g25,g31) = 1.5708
    c: Tangent(g25,g32) = 1.5708
    c: Tangent(g26,g32) = 1.5708
    c: Tangent(g26,g33) = 1.5708
    c: Tangent(g27,g33) = 1.5708
    c: Tangent(g27,g34) = -1.5708
    c: Tangent(g28,g34) = -1.5708
    c: Radius(g29) = 2
    c: Equal(g29,g30)
    c: PointOnObject(g23,g13)
    c: Equal(g30,g31)
    c: Tangent(g31,g21)
    c: Equal(g31,g32)
    c: Equal(g32,g33)
    c: Tangent(g33,g22)
    c: Coincident(g34,g14)
    c: Radius(g34) = 11
    c: DistanceX(g23,g23) = 7
    c: DistanceY(g23,g24) = 5
    c: DistanceY(g23,g26) = 10.5
    c: DistanceX(g26,g26) = 4
    c: DistanceX(g23,g14) = 4.5
FEATURE [PartDesign::Pad] Pad003
  Length = 6
  Length2 = 100
  Placement = pos=(0,0,0) rot=(1,0,0;1.5708rad)
  Profile = -> Sketch020
  Type = 0
FEATURE [Sketcher::SketchObject] Sketch021
  MapMode = 5
  Placement = pos=(0,-6,-1.8e-15) rot=(1,0,0;1.5708rad)
  expr: Constraints[9] = <<lockSketch>>.Constraints.lockFromEdge + 1mm
  expr: Constraints[8] = <<lockSketch>>.Constraints.lockLength
  sketch-geometry (4):
    g0: LineSegment StartX=-30 StartY=10 StartZ=0 EndX=30 EndY=10 EndZ=0
    g1: LineSegment StartX=30 StartY=10 StartZ=0 EndX=30 EndY=-12 EndZ=0
    g2: LineSegment StartX=30 StartY=-12 StartZ=0 EndX=-30 EndY=-12 EndZ=0
    g3: LineSegment StartX=-30 StartY=-12 StartZ=0 EndX=-30 EndY=10 EndZ=0
  constraints (11):
    c: Coincident(g0,g1)
    c: Coincident(g1,g2)
    c: Coincident(g2,g3)
    c: Coincident(g3,g0)
    c: Horizontal(g0)
    c: Vertical(g1)
    c: Vertical(g3)
    c: Symmetric(g1,g2,g-2)
    c: DistanceX(g2,g2) = 60
    c: DistanceY(g2,g-1) = 12
    c: DistanceY(g3,g3) = 22
FEATURE [PartDesign::Pocket] Pocket004
  BaseFeature = -> Pad003
  Length = 0.5
  Length2 = 100
  Placement = pos=(0,0,0) rot=(1,0,0;1.5708rad)
  Profile = -> Sketch021
  Type = 0
FEATURE [PartDesign::Body] Body007  label="Lock"
  Group = -> [Sketch020,Pad003,Sketch021,Pocket004]
  Origin = -> Origin007
  Tip = -> Pocket004
FEATURE [Sketcher::SketchObject] Sketch022
  MapMode = 5
  Placement = pos=(0,0,0) rot=(1,0,0;1.5708rad)
  Support = -> [XZ_Plane]
  expr: Constraints[30] = <<BushingSketch>>.Constraints.BushingHeight / 2
  expr: Constraints[9] = <<Base>>.Constraints.doorWidth
  expr: Constraints[8] = <<Base>>.Constraints.doorHeight
  sketch-geometry (23):
    g0: LineSegment [constr] StartX=-84 StartY=44.25 StartZ=0 EndX=84 EndY=44.25 EndZ=0
    g1: LineSegment [constr] StartX=84 StartY=44.25 StartZ=0 EndX=84 EndY=-44.25 EndZ=0
    g2: LineSegment [constr] StartX=84 StartY=-44.25 StartZ=0 EndX=-84 EndY=-44.25 EndZ=0
    g3: LineSegment [constr] StartX=-84 StartY=-44.25 StartZ=0 EndX=-84 EndY=44.25 EndZ=0
    g4: LineSegment [constr] StartX=-16.5 StartY=39.25 StartZ=0 EndX=28.5 EndY=39.25 EndZ=0
    g5: LineSegment [constr] StartX=28.5 StartY=39.25 StartZ=0 EndX=28.5 EndY=26.25 EndZ=0
    g6: LineSegment [constr] StartX=28.5 StartY=26.25 StartZ=0 EndX=-16.5 EndY=26.25 EndZ=0
    g7: LineSegment [constr] StartX=-16.5 StartY=26.25 StartZ=0 EndX=-16.5 EndY=39.25 EndZ=0
    g8: LineSegment [constr] StartX=-72 StartY=15.25 StartZ=0 EndX=-12 EndY=15.25 EndZ=0
    g9: LineSegment [constr] StartX=-12 StartY=15.25 StartZ=0 EndX=12 EndY=15.25 EndZ=0
    g10: LineSegment [constr] StartX=12 StartY=15.25 StartZ=0 EndX=42 EndY=15.25 EndZ=0
    g11: LineSegment [constr] StartX=19 StartY=-39.25 StartZ=0 EndX=-19 EndY=-39.25 EndZ=0
    g12: Circle CenterX=28.5 CenterY=39.25 CenterZ=0 NormalX=0 NormalY=0 NormalZ=1 AngleXU=0 Radius=2.1
    g13: Circle CenterX=28.5 CenterY=26.25 CenterZ=0 NormalX=0 NormalY=0 NormalZ=1 AngleXU=0 Radius=2.1
    g14: Circle CenterX=-16.5 CenterY=26.25 CenterZ=0 NormalX=0 NormalY=0 NormalZ=1 AngleXU=0 Radius=2.1
    g15: Circle CenterX=-16.5 CenterY=39.25 CenterZ=0 NormalX=0 NormalY=0 NormalZ=1 AngleXU=0 Radius=2.1
    g16: LineSegment [constr] StartX=-16.5 StartY=32.75 StartZ=0 EndX=28.5 EndY=32.75 EndZ=0
    g17: Circle CenterX=-72 CenterY=15.25 CenterZ=0 NormalX=0 NormalY=0 NormalZ=1 AngleXU=0 Radius=2.1
    g18: Circle CenterX=-12 CenterY=15.25 CenterZ=0 NormalX=0 NormalY=0 NormalZ=1 AngleXU=0 Radius=2.1
    g19: Circle CenterX=12 CenterY=15.25 CenterZ=0 NormalX=0 NormalY=0 NormalZ=1 AngleXU=0 Radius=2.1
    g20: Circle CenterX=42 CenterY=15.25 CenterZ=0 NormalX=0 NormalY=0 NormalZ=1 AngleXU=0 Radius=2.1
    g21: Circle CenterX=19 CenterY=-39.25 CenterZ=0 NormalX=0 NormalY=0 NormalZ=1 AngleXU=0 Radius=2.1
    g22: Circle CenterX=-19 CenterY=-39.25 CenterZ=0 NormalX=0 NormalY=0 NormalZ=1 AngleXU=0 Radius=2.1
  constraints (57):
    c: Coincident(g0,g1)
    c: Coincident(g1,g2)
    c: Coincident(g2,g3)
    c: Coincident(g3,g0)
    c: Horizontal(g0)
    c: Vertical(g3)
    c: Symmetric(g1,g2,g-2)
    c: Symmetric(g0,g1,g-1)
    c: DistanceY(g1,g1) = 88.5
    c: DistanceX(g2,g2) = 168
    c: Coincident(g4,g5)
    c: Coincident(g5,g6)
    c: Coincident(g6,g7)
    c: Coincident(g7,g4)
    c: Horizontal(g4)
    c: Horizontal(g6)
    c: Vertical(g5)
    c: Vertical(g7)
    c: Horizontal(g8)
    c: Coincident(g8,g9)
    c: Coincident(g9,g10)
    c: Horizontal(g10)
    c: Coincident(g12,g4)
    c: Coincident(g13,g5)
    c: Coincident(g14,g6)
    c: Coincident(g15,g4)
    c: DistanceY(g7,g7) = 13
    c: PointOnObject(g16,g7)
    c: PointOnObject(g16,g5)
    c: Symmetric(g13,g12,g16)
    c: DistanceY(g16,g0) = 11.5
    c: DistanceX(g15,g-1) = 16.5
    c: DistanceX(g-1,g12) = 28.5
    c: Diameter(g15) = 4.2
    c: Equal(g15,g14)
    c: Equal(g15,g12)
    c: Equal(g15,g13)
    c: Symmetric(g8,g9,g-2)
    c: DistanceX(g9,g9) = 24
    c: DistanceX(g8,g8) = 60
    c: DistanceY(g8,g0) = 29
    c: Coincident(g17,g8)
    c: Coincident(g18,g8)
    c: Coincident(g19,g9)
    c: Coincident(g20,g10)
    c: Diameter(g17) = 4.2
    c: Equal(g17,g18)
    c: Equal(g17,g19)
    c: Equal(g17,g20)
    c: Symmetric(g11,g11,g-2)
    c: Coincident(g21,g11)
    c: Coincident(g22,g11)
    c: Diameter(g22) = 4.2
    c: Equal(g22,g21)
    c: DistanceX(g11,g11) = 38
    c: DistanceY(g2,g22) = 5
    c: DistanceX(g10,g10) = 30
FEATURE [PartDesign::Hole] Hole
  BaseFeature = -> Pad
  Depth = 25
  DepthType = 0
  Diameter = 4.2
  DrillPoint = 1
  DrillPointAngle = 118
  HoleCutCountersinkAngle = 90
  HoleCutDepth = 0
  HoleCutDiameter = 0
  HoleCutType = 0
  ModelActualThread = false
  Placement = pos=(0,0,0) rot=(1,0,0;1.5708rad)
  Profile = -> Sketch022
  Tapered = false
  TaperedAngle = 90
  ThreadAngle = 0
  ThreadClass = 0
  ThreadCutOffInner = 0
  ThreadCutOffOuter = 0
  ThreadDirection = 0
  ThreadFit = 0
  ThreadPitch = 0
  ThreadSize = 0
  ThreadType = 0
  Threaded = false
FEATURE [PartDesign::Pad] Pad004
  BaseFeature = -> Hole
  Length = 3
  Length2 = 100
  Placement = pos=(0,0,0) rot=(1,0,0;1.5708rad)
  Profile = -> Sketch018
  Type = 0
FEATURE [Sketcher::SketchObject] Sketch023
  MapMode = 5
  Placement = pos=(0,0,0) rot=(1,0,0;1.5708rad)
  Support = -> [XZ_Plane]
  expr: Constraints[40] = Sketch018.Constraints[43]
  expr: Constraints[22] = Sketch018.Constraints[22]
  expr: Constraints[9] = Sketch018.Constraints[9]
  expr: Constraints[54] = Sketch018.Constraints[58]
  expr: Constraints[11] = Sketch018.Constraints[11]
  expr: Constraints[53] = Sketch018.Constraints[57]
  expr: Constraints[39] = Sketch018.Constraints[42]
  expr: Constraints[23] = Sketch018.Constraints[23]
  expr: Constraints[28] = Sketch018.Constraints[28]
  expr: Constraints[21] = Sketch018.Constraints[21]
  expr: Constraints[10] = Sketch018.Constraints[10]
  expr: Constraints[20] = Sketch018.Constraints[20]
  expr: Constraints[8] = Sketch018.Constraints[8]
  expr: Constraints[38] = Sketch018.Constraints[41]
  sketch-geometry (37):
    g0: LineSegment [constr] StartX=-84 StartY=10 StartZ=0 EndX=-14 EndY=10 EndZ=0
    g1: LineSegment [constr] StartX=-14 StartY=10 StartZ=0 EndX=-14 EndY=-30 EndZ=0
    g2: LineSegment [constr] StartX=-14 StartY=-30 StartZ=0 EndX=-84 EndY=-30 EndZ=0
    g3: LineSegment [constr] StartX=-84 StartY=-30 StartZ=0 EndX=-84 EndY=10 EndZ=0
    g4: LineSegment [constr] StartX=-81 StartY=7 StartZ=0 EndX=-17 EndY=7 EndZ=0
    g5: LineSegment [constr] StartX=-17 StartY=7 StartZ=0 EndX=-17 EndY=-27 EndZ=0
    g6: LineSegment [constr] StartX=-17 StartY=-27 StartZ=0 EndX=-81 EndY=-27 EndZ=0
    g7: LineSegment [constr] StartX=-81 StartY=-27 StartZ=0 EndX=-81 EndY=7 EndZ=0
    g8: Circle CenterX=-81 CenterY=7 CenterZ=0 NormalX=0 NormalY=0 NormalZ=1 AngleXU=0 Radius=0.8
    g9: Circle CenterX=-17 CenterY=7 CenterZ=0 NormalX=0 NormalY=0 NormalZ=1 AngleXU=0 Radius=0.8
    g10: Circle CenterX=-17 CenterY=-27 CenterZ=0 NormalX=0 NormalY=0 NormalZ=1 AngleXU=0 Radius=0.8
    g11: Circle CenterX=-81 CenterY=-27 CenterZ=0 NormalX=0 NormalY=0 NormalZ=1 AngleXU=0 Radius=0.8
    g12: LineSegment [constr] StartX=-84 StartY=-2.5 StartZ=0 EndX=-78.1 EndY=-2.5 EndZ=0
    g13: LineSegment [constr] StartX=-78.1 StartY=-15.5 StartZ=0 EndX=-84 EndY=-15.5 EndZ=0
    g14: LineSegment [constr] StartX=-84 StartY=-15.5 StartZ=0 EndX=-84 EndY=-2.5 EndZ=0
    g15: Circle [constr] CenterX=-17 CenterY=7 CenterZ=0 NormalX=0 NormalY=0 NormalZ=1 AngleXU=0 Radius=3
    g16: Circle [constr] CenterX=-81 CenterY=7 CenterZ=0 NormalX=0 NormalY=0 NormalZ=1 AngleXU=0 Radius=3
    g17: Circle [constr] CenterX=-81 CenterY=-27 CenterZ=0 NormalX=0 NormalY=0 NormalZ=1 AngleXU=0 Radius=3
    g18: Circle [constr] CenterX=-17 CenterY=-27 CenterZ=0 NormalX=0 NormalY=0 NormalZ=1 AngleXU=0 Radius=3
    g19: LineSegment [constr] StartX=-78.1 StartY=-2.5 StartZ=0 EndX=-74.1 EndY=-2.5 EndZ=0
    g20: LineSegment [constr] StartX=-74.1 StartY=-2.5 StartZ=0 EndX=-74.1 EndY=-15.5 EndZ=0
    g21: LineSegment [constr] StartX=-74.1 StartY=-15.5 StartZ=0 EndX=-78.1 EndY=-15.5 EndZ=0
    g22: LineSegment [constr] StartX=-78.1 StartY=-15.5 StartZ=0 EndX=-78.1 EndY=-2.5 EndZ=0
    g23: LineSegment StartX=-78.1 StartY=-17.5 StartZ=0 EndX=-84 EndY=-17.5 EndZ=0
    g24: LineSegment StartX=-84 StartY=-17.5 StartZ=0 EndX=-84 EndY=-1.5 EndZ=0
    g25: LineSegment StartX=-78.1 StartY=-17.5 StartZ=0 EndX=-78.1 EndY=-1.5 EndZ=0
    g26: LineSegment StartX=-78.1 StartY=-1.5 StartZ=0 EndX=-84 EndY=-1.5 EndZ=0
    g27: LineSegment [constr] StartX=-49 StartY=7 StartZ=0 EndX=-49 EndY=-27 EndZ=0
    g28: LineSegment [constr] StartX=-17 StartY=-10 StartZ=0 EndX=-81 EndY=-10 EndZ=0
    g29: LineSegment [constr] StartX=-82 StartY=3 StartZ=0 EndX=-16 EndY=3 EndZ=0
    g30: LineSegment [constr] StartX=-16 StartY=3 StartZ=0 EndX=-16 EndY=-23 EndZ=0
    g31: LineSegment [constr] StartX=-16 StartY=-23 StartZ=0 EndX=-82 EndY=-23 EndZ=0
    g32: LineSegment [constr] StartX=-82 StartY=-23 StartZ=0 EndX=-82 EndY=3 EndZ=0
    g33: Circle CenterX=-16 CenterY=3 CenterZ=0 NormalX=0 NormalY=0 NormalZ=1 AngleXU=0 Radius=0.8
    g34: Circle CenterX=-16 CenterY=-23 CenterZ=0 NormalX=0 NormalY=0 NormalZ=1 AngleXU=0 Radius=0.8
    g35: Circle CenterX=-82 CenterY=-23 CenterZ=0 NormalX=0 NormalY=0 NormalZ=1 AngleXU=0 Radius=0.8
    g36: Circle CenterX=-82 CenterY=3 CenterZ=0 NormalX=0 NormalY=0 NormalZ=1 AngleXU=0 Radius=0.8
  constraints (96):
    c: Coincident(g0,g1)
    c: Coincident(g1,g2)
    c: Coincident(g2,g3)
    c: Coincident(g3,g0)
    c: Horizontal(g0)
    c: Horizontal(g2)
    c: Vertical(g1)
    c: Vertical(g3)
    c: DistanceX(g2,g2) = 70
    c: DistanceY(g1,g1) = 40
    c: DistanceX(g0,g-1) = 84
    c: DistanceY(g-1,g0) = 10
    c: Coincident(g4,g5)
    c: Coincident(g5,g6)
    c: Coincident(g6,g7)
    c: Coincident(g7,g4)
    c: Horizontal(g4)
    c: Horizontal(g6)
    c: Vertical(g5)
    c: Vertical(g7)
    c: DistanceX(g4,g0) = 3
    c: DistanceY(g4,g0) = 3
    c: DistanceX(g0,g4) = 3
    c: DistanceY(g2,g6) = 3
    c: Coincident(g8,g4)
    c: Coincident(g9,g4)
    c: Coincident(g10,g5)
    c: Coincident(g11,g6)
    c: Diameter(g11) = 1.6
    c: Equal(g11,g8)
    c: Equal(g11,g9)
    c: Equal(g11,g10)
    c: Coincident(g13,g14)
    c: Coincident(g14,g12)
    c: Horizontal(g12)
    c: Horizontal(g13)
    c: Vertical(g14)
    c: PointOnObject(g12,g3)
    c: DistanceX(g13,g13) = 5.9
    c: DistanceY(g2,g13) = 14.5
    c: DistanceY(g13,g12) = 13
    c: Coincident(g15,g4)
    c: Coincident(g16,g4)
    c: Coincident(g17,g6)
    c: Coincident(g18,g5)
    c: Coincident(g19,g20)
    c: Coincident(g20,g21)
    c: Coincident(g21,g22)
    c: Coincident(g22,g19)
    c: Horizontal(g19)
    c: Horizontal(g21)
    c: Vertical(g20)
    c: Coincident(g19,g12)
    c: DistanceX(g19,g19) = 4
    c: Diameter(g16) = 6
    c: Equal(g16,g15)
    c: Equal(g16,g18)
    c: Equal(g16,g17)
    c: Coincident(g23,g24)
    c: Horizontal(g23)
    c: Vertical(g24)
    c: DistanceY(g23,g19) = 15
    c: Coincident(g25,g23)
    c: Vertical(g25)
    c: Coincident(g26,g25)
    c: Horizontal(g26)
    c: Coincident(g24,g26)
    c: PointOnObject(g24,g3)
    c: DistanceY(g12,g25) = 1
    c: PointOnObject(g13,g25)
    c: Vertical(g22)
    c: Coincident(g21,g13)
    c: PointOnObject(g27,g4)
    c: PointOnObject(g27,g6)
    c: Symmetric(g8,g9,g27)
    c: PointOnObject(g28,g5)
    c: PointOnObject(g28,g7)
    c: Symmetric(g10,g9,g28)
    c: Coincident(g29,g30)
    c: Coincident(g30,g31)
    c: Coincident(g31,g32)
    c: Coincident(g32,g29)
    c: Horizontal(g31)
    c: Vertical(g32)
    c: Symmetric(g29,g29,g27)
    c: Symmetric(g29,g30,g28)
    c: DistanceX(g29,g29) = 66
    c: DistanceY(g30,g30) = 26
    c: Coincident(g33,g29)
    c: Coincident(g34,g30)
    c: Coincident(g35,g31)
    c: Coincident(g36,g29)
    c: Diameter(g36) = 1.6
    c: Equal(g36,g35)
    c: Equal(g36,g33)
    c: Equal(g36,g34)
FEATURE [PartDesign::Pocket] Pocket005
  BaseFeature = -> Pad004
  Length = 5
  Length2 = 100
  Midplane = true
  Placement = pos=(0,0,0) rot=(1,0,0;1.5708rad)
  Profile = -> Sketch023
  Type = 1
FEATURE [Sketcher::SketchObject] Sketch025
  MapMode = 5
  Placement = pos=(0,-3,0) rot=(1,0,0;1.5708rad)
  Support = -> [Pocket005]
  sketch-geometry (4):
    g0: LineSegment StartX=-80 StartY=-2 StartZ=0 EndX=-72 EndY=-2 EndZ=0
    g1: LineSegment StartX=-72 StartY=-2 StartZ=0 EndX=-72 EndY=-16 EndZ=0
    g2: LineSegment StartX=-72 StartY=-16 StartZ=0 EndX=-80 EndY=-16 EndZ=0
    g3: LineSegment StartX=-80 StartY=-16 StartZ=0 EndX=-80 EndY=-2 EndZ=0
  constraints (12):
    c: Coincident(g0,g1)
    c: Coincident(g1,g2)
    c: Coincident(g2,g3)
    c: Coincident(g3,g0)
    c: Horizontal(g0)
    c: Horizontal(g2)
    c: Vertical(g1)
    c: Vertical(g3)
    c: DistanceY(g0,g-1) = 2
    c: DistanceX(g0,g0) = 8
    c: DistanceX(g0,g-1) = 80
    c: DistanceY(g1,g1) = 14
FEATURE [PartDesign::Pocket] Pocket006
  BaseFeature = -> Pocket005
  Length = 1
  Length2 = 100
  Placement = pos=(0,0,0) rot=(1,0,0;1.5708rad)
  Profile = -> Sketch025
  Type = 0
FEATURE [TechDraw::DrawSVGTemplate] Template
  EditableTexts = Designed_by_Name=Papamatthaiou M.; FC-Date=28/11/2019; FC-SC=1:1; FC-SHEET=1/1; FC-Title=PocketQube Bushing Holder; MATERIAL=NOTE-4; REV=A; ROUGHNESS=-; Subtitle=BushingHolder; TOLERANCES=DIN ISO 2768- mk; Weight=~28.3g
  Height = 210
  Orientation = 1
  Width = 297
FEATURE [TechDraw::DrawViewAnnotation] Annotation
  Font = DejaVu Sans
  LineSpace = 80
  LockPosition = false
  MaxWidth = -1
  Rotation = 0
  ScaleType = 0
  Text = Notes: | 1. Drill hole \u23005.0 THRU | 2. Mating hole (H7) for part Bushing | 3. Drill hole \u23004.4 THRU for M4 DIN7991 | 4. Material: Al 7075
  TextSize = 6
  TextStyle = 0
  X = 71.9634
  Y = 39.1652
FEATURE [TechDraw::DrawViewSymbol] Symbol
  LockPosition = false
  Rotation = 0
  ScaleType = 2
  Symbol = <blob: 2136 chars omitted>
  X = 253.294
  Y = 124.412
FEATURE [TechDraw::DrawViewSymbol] Symbol001
  LockPosition = false
  Rotation = 0
  ScaleType = 2
  Symbol = <blob: 3150 chars omitted>
  X = 182.346
  Y = 117.641
FEATURE [TechDraw::DrawSVGTemplate] Template001
  EditableTexts = Designed_by_Name=Papamatthaiou M.; FC-Date=28/11/2019; FC-SC=1:1; FC-SHEET=1/1; FC-Title=PocketQube Lock; MATERIAL=NOTE-4; REV=A; ROUGHNESS=-; Subtitle=Lock; TOLERANCES=DIN ISO 2768- mk; Weight=~17.2g
  Height = 210
  Orientation = 1
  Width = 297
FEATURE [TechDraw::DrawProjGroupItem] ProjItem002  label="Front001"
  CoarseView = false
  Direction = (0,-1,0)
  Focus = 100
  HardHidden = false
  IsoCount = 0
  IsoHidden = false
  IsoVisible = false
  LockPosition = true
  Perspective = false
  Rotation = 0
  RotationVector = (1,0,0)
  ScaleType = 2
  SeamHidden = false
  SeamVisible = false
  SmoothHidden = false
  SmoothVisible = false
  Source = -> [Body007]
  Type = 0
  X = 0
  Y = 0
FEATURE [TechDraw::DrawProjGroup] ProjGroup001
  Anchor = -> ProjItem002
  AutoDistribute = true
  LockPosition = false
  ProjectionType = 1
  Rotation = 0
  ScaleType = 2
  Source = -> [Body007]
  Views = -> [ProjItem002]
  X = 105.691
  Y = 133.944
  spacingX = 15
  spacingY = 15
FEATURE [TechDraw::DrawViewPart] View002
  CoarseView = false
  Direction = (0.357,-0.646,0.674)
  Focus = 100
  HardHidden = false
  IsoCount = 0
  IsoHidden = false
  IsoVisible = false
  LockPosition = false
  Perspective = false
  Rotation = 0
  ScaleType = 0
  SeamHidden = false
  SeamVisible = false
  SmoothHidden = false
  SmoothVisible = false
  Source = -> [Body007]
  X = 253.923
  Y = 178.857
FEATURE [TechDraw::DrawViewDimension] Dimension012
  Arbitrary = false
  FormatSpec = (Note-1) ⌀%.2f
  LockPosition = false
  MeasureType = 1
  OverTolerance = 0
  References2D = -> [ProjItem002]
  Rotation = 0
  ScaleType = 0
  Type = 5
  UnderTolerance = 0
  X = -55.3334
  Y = -20.6436
FEATURE [TechDraw::DrawViewDimension] Dimension013
  Arbitrary = false
  FormatSpec = (Note-2) ⌀%.2f
  LockPosition = false
  MeasureType = 1
  OverTolerance = 0
  References2D = -> [ProjItem002]
  Rotation = 0
  ScaleType = 0
  Type = 5
  UnderTolerance = 0
  X = -38.8556
  Y = 21.6944
FEATURE [TechDraw::DrawViewDimension] Dimension014
  Arbitrary = false
  FormatSpec = (Note-3) ⌀%.2f
  LockPosition = false
  MeasureType = 1
  OverTolerance = 0
  References2D = -> [ProjItem002]
  Rotation = 0
  ScaleType = 0
  Type = 5
  UnderTolerance = 0
  X = 40.4746
  Y = 26.7132
FEATURE [TechDraw::DrawViewAnnotation] Annotation001
  Font = DejaVu Sans
  LineSpace = 80
  LockPosition = false
  MaxWidth = -1
  Rotation = 0
  ScaleType = 0
  Text = Notes: | 1. Drill hole \u23004.2 THRU | 2. Drill hole \u23005.0 THRU | 3. Drill hole \u23005.0 THRU | 4. Material: Al 7075
  TextSize = 6
  TextStyle = 0
  X = 48.4469
  Y = 39.1398
FEATURE [TechDraw::DrawViewDimension] Dimension015
  Arbitrary = false
  FormatSpec = %.2f
  LockPosition = false
  MeasureType = 1
  OverTolerance = 0.1
  References2D = -> [ProjItem002]
  Rotation = 0
  ScaleType = 0
  Type = 2
  UnderTolerance = -0.1
  X = 47.136
  Y = -5.09369
FEATURE [TechDraw::DrawViewDimension] Dimension016
  Arbitrary = false
  FormatSpec = %.2f
  LockPosition = false
  MeasureType = 1
  OverTolerance = 0.1
  References2D = -> [ProjItem002]
  Rotation = 0
  ScaleType = 0
  Type = 1
  UnderTolerance = -0.1
  X = 14.8126
  Y = -34.5127
FEATURE [TechDraw::DrawPage] Page001
  KeepUpdated = true
  ProjectionType = 0
  Template = -> Template001
  Views = -> [ProjGroup001,View002,Dimension012,Dimension013,Dimension014,Annotation001,Dimension015,Dimension016]
FEATURE [Sketcher::SketchObject] Sketch027
  MapMode = 5
  Placement = pos=(-78.1,0,0) rot=(0.707107,0,-0.707107;3.14159rad)
  Support = -> [Pocket006]
  sketch-geometry (2):
    g0: Circle CenterX=5.7 CenterY=0.5 CenterZ=0 NormalX=0 NormalY=0 NormalZ=1 AngleXU=0 Radius=1
    g1: Circle CenterX=12.2 CenterY=0.5 CenterZ=0 NormalX=0 NormalY=0 NormalZ=1 AngleXU=0 Radius=1
  constraints (6):
    c: DistanceX(g-1,g0) = 5.7
    c: Horizontal(g0,g1)
    c: Equal(g0,g1)
    c: Diameter(g0) = 2
    c: DistanceX(g0,g1) = 6.5
    c: DistanceY(g-1,g1) = 0.5
FEATURE [PartDesign::Hole] Hole004
  BaseFeature = -> Pocket006
  Depth = 3
  DepthType = 0
  Diameter = 1.6
  DrillPoint = 1
  DrillPointAngle = 118
  HoleCutCountersinkAngle = 90
  HoleCutDepth = 0
  HoleCutDiameter = 2
  HoleCutType = 0
  ModelActualThread = false
  Placement = pos=(0,0,0) rot=(1,0,0;1.5708rad)
  Profile = -> Sketch027
  Tapered = false
  TaperedAngle = 90
  ThreadAngle = 60
  ThreadClass = 0
  ThreadCutOffInner = 0.0433013
  ThreadCutOffOuter = 0.0866025
  ThreadDirection = 1
  ThreadFit = 0
  ThreadPitch = 0.4
  ThreadSize = 1
  ThreadType = 1
  Threaded = true
FEATURE [PartDesign::Body] Body  label="Door"
  Group = -> [Sketch,Sketch001,Pad,Hole,Sketch022,Sketch018,Pad004,Sketch023,Pocket005,Sketch025,Pocket006,Sketch027,Hole004]
  Origin = -> Origin
  Tip = -> Hole004
FEATURE [Sketcher::SketchObject] Sketch010
  MapMode = 5
  Placement = pos=(0,0,0) rot=(1,0,0;1.5708rad)
  Support = -> [XZ_Plane002]
  sketch-geometry (18):
    g0: LineSegment StartX=-24 StartY=-7 StartZ=0 EndX=-24 EndY=-3 EndZ=0
    g1: ArcOfCircle CenterX=-21 CenterY=-3 CenterZ=0 NormalX=0 NormalY=0 NormalZ=1 AngleXU=0 Radius=3 StartAngle=1.5708 EndAngle=3.14159
    g2: LineSegment StartX=-21 StartY=0 StartZ=0 EndX=-12 EndY=0 EndZ=0
    g3: ArcOfCircle CenterX=-12 CenterY=7.5 CenterZ=0 NormalX=0 NormalY=0 NormalZ=1 AngleXU=0 Radius=7.5 StartAngle=4.71239 EndAngle=5.63968
    g4: LineSegment StartX=24 StartY=-1.177e-13 StartZ=0 EndX=33 EndY=-1.177e-13 EndZ=0
    g5: ArcOfCircle CenterX=33 CenterY=-3 CenterZ=0 NormalX=0 NormalY=0 NormalZ=1 AngleXU=0 Radius=3 StartAngle=5.689e-13 EndAngle=1.5708
    g6: LineSegment StartX=36 StartY=-3 StartZ=0 EndX=36 EndY=-7 EndZ=0
    g7: LineSegment StartX=36 StartY=-7 StartZ=0 EndX=-24 EndY=-7 EndZ=0
    g8: Circle CenterX=0 CenterY=-1 CenterZ=0 NormalX=0 NormalY=0 NormalZ=1 AngleXU=0 Radius=4
    g9: Circle [constr] CenterX=0 CenterY=-1 CenterZ=0 NormalX=0 NormalY=0 NormalZ=1 AngleXU=0 Radius=5
    g10: Circle CenterX=12 CenterY=4 CenterZ=0 NormalX=0 NormalY=0 NormalZ=1 AngleXU=0 Radius=2.5
    g11: Circle [constr] CenterX=12 CenterY=4 CenterZ=0 NormalX=0 NormalY=0 NormalZ=1 AngleXU=0 Radius=5
    g12: Circle [constr] CenterX=0 CenterY=-1 CenterZ=0 NormalX=0 NormalY=0 NormalZ=1 AngleXU=0 Radius=2.5
    g13: ArcOfCircle CenterX=24 CenterY=7.5 CenterZ=0 NormalX=0 NormalY=0 NormalZ=1 AngleXU=0 Radius=7.5 StartAngle=3.42539 EndAngle=4.71239
    g14: ArcOfCircle CenterX=-9e-16 CenterY=-1.5 CenterZ=0 NormalX=0 NormalY=0 NormalZ=1 AngleXU=0 Radius=7.5 StartAngle=1.5708 EndAngle=2.49809
    g15: LineSegment StartX=-4e-16 StartY=6 StartZ=0 EndX=5.755 EndY=6 EndZ=0
    g16: ArcOfCircle CenterX=12 CenterY=4 CenterZ=0 NormalX=0 NormalY=0 NormalZ=1 AngleXU=0 Radius=5 StartAngle=0.283794 EndAngle=2.46646
    g17: ArcOfCircle CenterX=5.755 CenterY=9 CenterZ=0 NormalX=0 NormalY=0 NormalZ=1 AngleXU=0 Radius=3 StartAngle=4.71239 EndAngle=5.60805
  constraints (47):
    c: Vertical(g0)
    c: Tangent(g0,g1) = 1.5708
    c: Tangent(g1,g2) = 1.5708
    c: Tangent(g2,g3) = -1.5708
    c: Tangent(g4,g5) = 1.5708
    c: Vertical(g6)
    c: Coincident(g7,g6)
    c: Coincident(g0,g7)
    c: Equal(g5,g1)
    c: Tangent(g6,g5) = 1.5708
    c: Horizontal(g2)
    c: Horizontal(g4)
    c: Equal(g0,g6)
    c: Diameter(g8) = 8
    c: Diameter(g9) = 10
    c: Radius(g1) = 3
    c: DistanceY(g0,g1) = 7
    c: PointOnObject(g2,g-1)
    c: Horizontal(g7)
    c: Diameter(g10) = 5
    c: Coincident(g11,g10)
    c: Diameter(g11) = 10
    c: Diameter(g12) = 5
    c: Tangent(g13,g4) = -1.5708
    c: Equal(g13,g3)
    c: Equal(g4,g2)
    c: Tangent(g14,g3) = 1.5708
    c: Coincident(g8,g9)
    c: PointOnObject(g8,g-2)
    c: DistanceY(g8,g-1) = 1
    c: DistanceX(g7,g7) = 60
    c: DistanceX(g8,g10) = 12
    c: DistanceX(g0,g8) = 24
    c: Coincident(g12,g8)
    c: DistanceX(g10,g6) = 24
    c: DistanceX(g0,g2) = 12
    c: DistanceY(g-1,g10) = 4
    c: Horizontal(g15)
    c: Tangent(g15,g14) = 1.5708
    c: Tangent(g17,g16) = 1.5708
    c: Tangent(g17,g15) = -1.5708
    c: Tangent(g16,g13) = 1.5708
    c: Coincident(g16,g10)
    c: Radius(g16) = 5
    c: Radius(g17) = 3
    c: PointOnObject(g14,g-2)
    c: DistanceY(g-1,g14) = 6
FEATURE [PartDesign::Pad] Pad001
  Length = 23
  Length2 = 100
  Placement = pos=(0,0,0) rot=(1,0,0;1.5708rad)
  Profile = -> Sketch010
  Reversed = true
  Type = 0
  expr: Length = <<BushingSketch>>.Constraints.BushingHeight
FEATURE [Sketcher::SketchObject] Sketch011
  MapMode = 5
  Placement = pos=(0,0,0) rot=(1,0,0;1.5708rad)
  Support = -> [XZ_Plane002]
  sketch-geometry (1):
    g0: Circle CenterX=0 CenterY=-1 CenterZ=0 NormalX=0 NormalY=0 NormalZ=1 AngleXU=0 Radius=5
  constraints (3):
    c: PointOnObject(g0,g-2)
    c: DistanceY(g-1,g0) = -1
    c: Diameter(g0) = 10
FEATURE [PartDesign::Pocket] Pocket001
  BaseFeature = -> Pad001
  Length = 3
  Length2 = 100
  Placement = pos=(0,0,0) rot=(1,0,0;1.5708rad)
  Profile = -> Sketch011
  Type = 0
FEATURE [Sketcher::SketchObject] Sketch019
  MapMode = 5
  Placement = pos=(0,0,0) rot=(1,0,0;1.5708rad)
  Support = -> [XZ_Plane002]
  expr: Constraints[46] = Sketch010.Constraints[46]
  expr: Constraints[43] = Sketch010.Constraints[43]
  expr: Constraints[36] = Sketch010.Constraints[36]
  expr: Constraints[35] = Sketch010.Constraints[35]
  expr: Constraints[32] = Sketch010.Constraints[32]
  expr: Constraints[29] = Sketch010.Constraints[29]
  expr: Constraints[31] = Sketch010.Constraints[31]
  expr: Constraints[30] = Sketch010.Constraints[30]
  expr: Constraints[21] = Sketch010.Constraints[21]
  expr: Constraints[19] = Sketch010.Constraints[19]
  expr: Constraints[44] = Sketch010.Constraints[44]
  expr: Constraints[16] = Sketch010.Constraints[16]
  expr: Constraints[15] = Sketch010.Constraints[15]
  expr: Constraints[22] = Sketch010.Constraints[22]
  expr: Constraints[14] = Sketch010.Constraints[14]
  expr: Constraints[13] = Sketch010.Constraints[13]
  sketch-geometry (24):
    g0: LineSegment [constr] StartX=-24 StartY=-7 StartZ=0 EndX=-24 EndY=-3 EndZ=0
    g1: ArcOfCircle [constr] CenterX=-21 CenterY=-3 CenterZ=0 NormalX=0 NormalY=0 NormalZ=1 AngleXU=0 Radius=3 StartAngle=1.5708 EndAngle=3.14159
    g2: LineSegment [constr] StartX=-21 StartY=0 StartZ=0 EndX=-12 EndY=0 EndZ=0
    g3: ArcOfCircle [constr] CenterX=-12 CenterY=7.5 CenterZ=0 NormalX=0 NormalY=0 NormalZ=1 AngleXU=0 Radius=7.5 StartAngle=4.71239 EndAngle=5.63968
    g4: LineSegment [constr] StartX=24 StartY=1.803e-13 StartZ=0 EndX=33 EndY=1.803e-13 EndZ=0
    g5: ArcOfCircle [constr] CenterX=33 CenterY=-3 CenterZ=0 NormalX=0 NormalY=0 NormalZ=1 AngleXU=0 Radius=3 StartAngle=5.689e-13 EndAngle=1.5708
    g6: LineSegment [constr] StartX=36 StartY=-3 StartZ=0 EndX=36 EndY=-7 EndZ=0
    g7: LineSegment [constr] StartX=36 StartY=-7 StartZ=0 EndX=-24 EndY=-7 EndZ=0
    g8: Circle [constr] CenterX=0 CenterY=-1 CenterZ=0 NormalX=0 NormalY=0 NormalZ=1 AngleXU=0 Radius=4
    g9: Circle [constr] CenterX=0 CenterY=-1 CenterZ=0 NormalX=0 NormalY=0 NormalZ=1 AngleXU=0 Radius=5
    g10: Circle [constr] CenterX=12 CenterY=4 CenterZ=0 NormalX=0 NormalY=0 NormalZ=1 AngleXU=0 Radius=2.5
    g11: Circle [constr] CenterX=12 CenterY=4 CenterZ=0 NormalX=0 NormalY=0 NormalZ=1 AngleXU=0 Radius=5
    g12: Circle [constr] CenterX=0 CenterY=-1 CenterZ=0 NormalX=0 NormalY=0 NormalZ=1 AngleXU=0 Radius=2.5
    g13: ArcOfCircle [constr] CenterX=24 CenterY=7.5 CenterZ=0 NormalX=0 NormalY=0 NormalZ=1 AngleXU=0 Radius=7.5 StartAngle=3.42539 EndAngle=4.71239
    g14: ArcOfCircle [constr] CenterX=-9e-16 CenterY=-1.5 CenterZ=0 NormalX=0 NormalY=0 NormalZ=1 AngleXU=0 Radius=7.5 StartAngle=1.5708 EndAngle=2.49809
    g15: LineSegment [constr] StartX=0 StartY=6 StartZ=0 EndX=5.755 EndY=6 EndZ=0
    g16: ArcOfCircle [constr] CenterX=12 CenterY=4 CenterZ=0 NormalX=0 NormalY=0 NormalZ=1 AngleXU=0 Radius=5 StartAngle=0.283794 EndAngle=2.46646
    g17: ArcOfCircle [constr] CenterX=5.755 CenterY=9 CenterZ=0 NormalX=0 NormalY=0 NormalZ=1 AngleXU=0 Radius=3 StartAngle=4.71239 EndAngle=5.60805
    g18: ArcOfCircle CenterX=-9e-16 CenterY=-1.5 CenterZ=0 NormalX=0 NormalY=0 NormalZ=1 AngleXU=0 Radius=7.5 StartAngle=0.442911 EndAngle=1.5708
    g19: ArcOfCircle CenterX=9.48683 CenterY=3 CenterZ=0 NormalX=0 NormalY=0 NormalZ=1 AngleXU=0 Radius=3 StartAngle=3.5845 EndAngle=4.71239
    g20: LineSegment StartX=9.48683 StartY=0 StartZ=0 EndX=24 EndY=1.803e-13 EndZ=0
    g21: LineSegment StartX=24 StartY=9 StartZ=0 EndX=0 EndY=9 EndZ=0
    g22: LineSegment StartX=0 StartY=9 StartZ=0 EndX=0 EndY=6 EndZ=0
    g23: LineSegment StartX=24 StartY=9 StartZ=0 EndX=24 EndY=1.812e-13 EndZ=0
  constraints (62):
    c: Vertical(g0)
    c: Tangent(g0,g1) = 1.5708
    c: Tangent(g1,g2) = 1.5708
    c: Tangent(g2,g3) = -1.5708
    c: Tangent(g4,g5) = 1.5708
    c: Vertical(g6)
    c: Coincident(g7,g6)
    c: Coincident(g0,g7)
    c: Equal(g5,g1)
    c: Tangent(g6,g5) = 1.5708
    c: Horizontal(g2)
    c: Horizontal(g4)
    c: Equal(g0,g6)
    c: Diameter(g8) = 8
    c: Diameter(g9) = 10
    c: Radius(g1) = 3
    c: DistanceY(g0,g1) = 7
    c: PointOnObject(g2,g-1)
    c: Horizontal(g7)
    c: Diameter(g10) = 5
    c: Coincident(g11,g10)
    c: Diameter(g11) = 10
    c: Diameter(g12) = 5
    c: Tangent(g13,g4) = -1.5708
    c: Equal(g13,g3)
    c: Equal(g4,g2)
    c: Tangent(g14,g3) = 1.5708
    c: Coincident(g8,g9)
    c: PointOnObject(g8,g-2)
    c: DistanceY(g8,g-1) = 1
    c: DistanceX(g7,g7) = 60
    c: DistanceX(g8,g10) = 12
    c: DistanceX(g0,g8) = 24
    c: Coincident(g12,g8)
    c: DistanceX(g10,g6) = 24
    c: DistanceX(g0,g2) = 12
    c: DistanceY(g-1,g10) = 4
    c: Horizontal(g15)
    c: Tangent(g15,g14) = 1.5708
    c: Tangent(g17,g16) = 1.5708
    c: Tangent(g17,g15) = -1.5708
    c: Tangent(g16,g13) = 1.5708
    c: Coincident(g16,g10)
    c: Radius(g16) = 5
    c: Radius(g17) = 3
    c: PointOnObject(g14,g-2)
    c: DistanceY(g-1,g14) = 6
    c: Tangent(g19,g-1) = -1.5708
    c: Tangent(g19,g18) = 1.5708
    c: Coincident(g20,g19)
    c: Equal(g18,g14)
    c: Coincident(g20,g4)
    c: Tangent(g18,g14) = -1.5708
    c: Horizontal(g21)
    c: Tangent(g21,g16)
    c: PointOnObject(g21,g-2)
    c: Coincident(g22,g21)
    c: Coincident(g22,g18)
    c: Coincident(g23,g21)
    c: Coincident(g23,g20)
    c: Vertical(g23)
    c: Radius(g19) = 3
FEATURE [PartDesign::Pocket] Pocket003
  BaseFeature = -> Pocket001
  Length = 14
  Length2 = 100
  Placement = pos=(0,0,0) rot=(1,0,0;1.5708rad)
  Profile = -> Sketch019
  Type = 0
FEATURE [Sketcher::SketchObject] Sketch012  label="BushingMountingSketch"
  MapMode = 5
  Support = -> [XY_Plane002]
  expr: Constraints[19] = <<BushingSketch>>.Constraints.BushingHeight / 2
  sketch-geometry (9):
    g0: Circle CenterX=-16.5 CenterY=18 CenterZ=0 NormalX=0 NormalY=0 NormalZ=1 AngleXU=0 Radius=2
    g1: Circle CenterX=28.5 CenterY=18 CenterZ=0 NormalX=0 NormalY=0 NormalZ=1 AngleXU=0 Radius=2
    g2: LineSegment [constr] StartX=-16.5 StartY=18 StartZ=0 EndX=28.5 EndY=18 EndZ=0
    g3: LineSegment [constr] StartX=28.5 StartY=18 StartZ=0 EndX=28.5 EndY=5 EndZ=0
    g4: LineSegment [constr] StartX=28.5 StartY=5 StartZ=0 EndX=-16.5 EndY=5 EndZ=0
    g5: LineSegment [constr] StartX=-16.5 StartY=5 StartZ=0 EndX=-16.5 EndY=18 EndZ=0
    g6: Circle CenterX=28.5 CenterY=5 CenterZ=0 NormalX=0 NormalY=0 NormalZ=1 AngleXU=0 Radius=2
    g7: Circle CenterX=-16.5 CenterY=5 CenterZ=0 NormalX=0 NormalY=0 NormalZ=1 AngleXU=0 Radius=2
    g8: LineSegment [constr] StartX=-16.5 StartY=11.5 StartZ=0 EndX=28.5 EndY=11.5 EndZ=0
  constraints (23):
    c: Diameter(g1) = 4
    c: Equal(g1,g0)
    c: Coincident(g2,g3)
    c: Coincident(g3,g4)
    c: Coincident(g4,g5)
    c: Coincident(g5,g2)
    c: Horizontal(g4)
    c: Vertical(g3)
    c: Vertical(g5)
    c: Coincident(g2,g0)
    c: Coincident(g2,g1)
    c: Coincident(g6,g3)
    c: Coincident(g7,g4)
    c: Equal(g7,g6)
    c: Equal(g6,g1)
    c: DistanceY(g3,g3) = 13  'BoushingMountingX'
    c: PointOnObject(g8,g5)
    c: PointOnObject(g8,g3)
    c: Symmetric(g6,g1,g8)
    c: DistanceY(g-1,g8) = 11.5
    c: DistanceX(g7,g-1) = 16.5
    c: DistanceX(g-1,g6) = 28.5
    c: Equal(g5,g3)
FEATURE [PartDesign::Hole] Hole003
  BaseFeature = -> Pocket003
  Depth = 25
  DepthType = 0
  Diameter = 4.4
  DrillPoint = 1
  DrillPointAngle = 118
  HoleCutCountersinkAngle = 90
  HoleCutDepth = 0
  HoleCutDiameter = 8
  HoleCutType = 2
  ModelActualThread = false
  Placement = pos=(0,0,0) rot=(1,0,0;1.5708rad)
  Profile = -> Sketch012
  Tapered = false
  TaperedAngle = 90
  ThreadAngle = 0
  ThreadClass = 0
  ThreadCutOffInner = 0
  ThreadCutOffOuter = 0
  ThreadDirection = 0
  ThreadFit = 0
  ThreadPitch = 0
  ThreadSize = 5
  ThreadType = 1
  Threaded = false
FEATURE [PartDesign::Body] Body002  label="BushingHolder"
  Group = -> [Sketch010,Pad001,Sketch011,Pocket001,Sketch019,Pocket003,Sketch012,Hole003]
  Origin = -> Origin002
  Tip = -> Hole003
FEATURE [TechDraw::DrawProjGroupItem] ProjItem  label="Front"
  CoarseView = false
  Direction = (0,-1,0)
  Focus = 100
  HardHidden = false
  IsoCount = 0
  IsoHidden = false
  IsoVisible = false
  LockPosition = true
  Perspective = false
  Rotation = 0
  RotationVector = (1,0,0)
  ScaleType = 2
  SeamHidden = false
  SeamVisible = false
  SmoothHidden = false
  SmoothVisible = false
  Source = -> [Body002]
  Type = 0
  X = 0
  Y = 0
FEATURE [TechDraw::DrawProjGroupItem] ProjItem001  label="Top"
  CoarseView = false
  Direction = (0,0,1)
  Focus = 100
  HardHidden = false
  IsoCount = 0
  IsoHidden = false
  IsoVisible = false
  LockPosition = true
  Perspective = false
  Rotation = 0
  RotationVector = (1,0,0)
  ScaleType = 2
  SeamHidden = false
  SeamVisible = false
  SmoothHidden = false
  SmoothVisible = false
  Source = -> [Body002]
  Type = 4
  X = 0
  Y = -61.0274
FEATURE [TechDraw::DrawProjGroup] ProjGroup
  Anchor = -> ProjItem
  AutoDistribute = true
  LockPosition = false
  ProjectionType = 1
  Rotation = 0
  ScaleType = 2
  Source = -> [Body002]
  Views = -> [ProjItem,ProjItem001]
  X = 100.401
  Y = 165.992
  spacingX = 15
  spacingY = 15
FEATURE [TechDraw::DrawViewPart] View
  CoarseView = false
  Direction = (0.444,-0.72,0.533)
  Focus = 100
  HardHidden = false
  IsoCount = 0
  IsoHidden = false
  IsoVisible = false
  LockPosition = false
  Perspective = false
  Rotation = 0
  ScaleType = 0
  SeamHidden = false
  SeamVisible = false
  SmoothHidden = false
  SmoothVisible = false
  Source = -> [Body002]
  X = 250.977
  Y = 179.73
FEATURE [TechDraw::DrawViewDimension] Dimension
  Arbitrary = false
  FormatSpec = (Note-2) ⌀%.2fH7
  LockPosition = false
  MeasureType = 1
  OverTolerance = 0
  References2D = -> [ProjItem]
  Rotation = 0
  ScaleType = 0
  Type = 5
  UnderTolerance = 0
  X = -43.369
  Y = 22.272
FEATURE [TechDraw::DrawViewDimension] Dimension002
  Arbitrary = false
  FormatSpec = (Note-1) ⌀%.2f
  LockPosition = false
  MeasureType = 1
  OverTolerance = 0
  References2D = -> [ProjItem]
  Rotation = 0
  ScaleType = 0
  Type = 5
  UnderTolerance = 0
  X = 29.3019
  Y = 19.3283
FEATURE [TechDraw::DrawViewDimension] Dimension003
  Arbitrary = false
  FormatSpec = (Note-4) ⌀%.2f
  LockPosition = false
  MeasureType = 1
  OverTolerance = 0
  References2D = -> [ProjItem001]
  Rotation = 0
  ScaleType = 0
  Type = 5
  UnderTolerance = 0
  X = -12.3298
  Y = 22.2011
FEATURE [TechDraw::DrawViewDimension] Dimension006
  Arbitrary = false
  FormatSpec = %.2f
  LockPosition = false
  MeasureType = 1
  OverTolerance = 0.1
  References2D = -> [ProjItem]
  Rotation = 0
  ScaleType = 0
  Type = 2
  UnderTolerance = -0.1
  X = 38.6178
  Y = -24.1167
FEATURE [TechDraw::DrawViewDimension] Dimension007
  Arbitrary = false
  FormatSpec = %.2f
  LockPosition = false
  MeasureType = 1
  OverTolerance = 0.1
  References2D = -> [ProjItem]
  Rotation = 0
  ScaleType = 0
  Type = 1
  UnderTolerance = -0.1
  X = 11.0513
  Y = -23.2042
FEATURE [TechDraw::DrawViewDimension] Dimension009
  Arbitrary = false
  FormatSpec = %.2f
  LockPosition = false
  MeasureType = 1
  OverTolerance = 0
  References2D = -> [ProjItem001]
  Rotation = 0
  ScaleType = 0
  Type = 2
  UnderTolerance = -0.1
  X = 50.1471
  Y = -21.5434
FEATURE [TechDraw::DrawViewDimension] Dimension010
  Arbitrary = false
  FormatSpec = %.2f
  LockPosition = false
  MeasureType = 1
  OverTolerance = 0
  References2D = -> [ProjItem001]
  Rotation = 0
  ScaleType = 0
  Type = 2
  UnderTolerance = -0.1
  X = 39.6679
  Y = -23.0478
FEATURE [TechDraw::DrawViewSection] DrawViewSection  label="Section A - A"
  BaseView = -> ProjItem
  CoarseView = false
  Direction = (0,0,-1)
  FileHatchPattern = <path>
  Focus = 100
  FuseBeforeCut = true
  HardHidden = false
  HatchScale = 1
  IsoCount = 0
  IsoHidden = false
  IsoVisible = false
  LockPosition = false
  NameGeomPattern = Diamond
  Perspective = false
  Rotation = 0
  ScaleType = 0
  SeamHidden = false
  SeamVisible = false
  SectionDirection = 2
  SectionNormal = (0,0,-1)
  SectionOrigin = (6,9.5,1)
  SectionSymbol = A
  SmoothHidden = false
  SmoothVisible = false
  Source = -> [Body002]
  X = 227.874
  Y = 121.242
FEATURE [TechDraw::DrawViewDimension] Dimension011
  Arbitrary = false
  FormatSpec = ⌀%.2f
  LockPosition = false
  MeasureType = 1
  OverTolerance = 0.2
  References2D = -> [ProjItem]
  Rotation = 0
  ScaleType = 0
  Type = 5
  UnderTolerance = 0
  X = -50.111
  Y = -14.9195
FEATURE [TechDraw::DrawPage] Page
  KeepUpdated = true
  ProjectionType = 0
  Template = -> Template
  Views = -> [ProjGroup,View,Dimension,Dimension002,Dimension003,Dimension006,Dimension007,Dimension009,Dimension010,Annotation,Symbol,DrawViewSection,Symbol001,Dimension011]
FEATURE [TechDraw::DrawSVGTemplate] Template002
  EditableTexts = Designed_by_Name=Papamatthaiou M.; FC-Date=2/12/2019; FC-SC=1:1; FC-SHEET=1/1; FC-Title=PicoBus Door; MATERIAL=NOTE-1; REV=A; ROUGHNESS=-; Subtitle=Door; TOLERANCES=DIN ISO 2768- mk; Weight=~206.2g
  Height = 210
  Orientation = 1
  Width = 297
FEATURE [TechDraw::DrawProjGroupItem] ProjItem003  label="Front002"
  CoarseView = false
  Direction = (0,-1,0)
  Focus = 100
  HardHidden = false
  IsoCount = 0
  IsoHidden = false
  IsoVisible = false
  LockPosition = true
  Perspective = false
  Rotation = 0
  RotationVector = (1,0,0)
  ScaleType = 2
  SeamHidden = false
  SeamVisible = false
  SmoothHidden = false
  SmoothVisible = false
  Source = -> [Body]
  Type = 0
  X = 0
  Y = 0
FEATURE [TechDraw::DrawProjGroupItem] ProjItem005  label="Left"
  CoarseView = false
  Direction = (-1,-1e-16,0)
  Focus = 100
  HardHidden = false
  IsoCount = 0
  IsoHidden = false
  IsoVisible = false
  LockPosition = false
  Perspective = false
  Rotation = 0
  RotationVector = (1e-16,-1,0)
  ScaleType = 2
  SeamHidden = false
  SeamVisible = false
  SmoothHidden = false
  SmoothVisible = false
  Source = -> [Body]
  Type = 1
  X = 121.393
  Y = 0
FEATURE [TechDraw::DrawProjGroup] ProjGroup002
  Anchor = -> ProjItem003
  AutoDistribute = false
  LockPosition = false
  ProjectionType = 1
  Rotation = 0
  ScaleType = 2
  Source = -> [Body]
  Views = -> [ProjItem003,ProjItem005]
  X = 113.256
  Y = 133.594
  spacingX = 2
  spacingY = 15
FEATURE [TechDraw::DrawViewDimension] Dimension020
  Arbitrary = false
  FormatSpec = (Note-4) ⌀%.2f
  LockPosition = false
  MeasureType = 1
  OverTolerance = 0
  References2D = -> [ProjItem005]
  Rotation = 0
  ScaleType = 0
  Type = 5
  UnderTolerance = 0
  X = 26.1975
  Y = -1.23214
FEATURE [TechDraw::DrawViewDimension] Dimension021
  Arbitrary = false
  FormatSpec = (Note-2) ⌀%.2f
  LockPosition = false
  MeasureType = 1
  OverTolerance = 0
  References2D = -> [ProjItem003]
  Rotation = 0
  ScaleType = 0
  Type = 5
  UnderTolerance = 0
  X = -49.7203
  Y = 4.84156
FEATURE [TechDraw::DrawViewDimension] Dimension022
  Arbitrary = false
  FormatSpec = (Note-3) ⌀%.2f
  LockPosition = false
  MeasureType = 1
  OverTolerance = 0
  References2D = -> [ProjItem003]
  Rotation = 0
  ScaleType = 0
  Type = 5
  UnderTolerance = 0
  X = -48.3349
  Y = 26.9008
FEATURE [TechDraw::DrawViewDimension] Dimension023
  Arbitrary = false
  FormatSpec = %.2f
  LockPosition = false
  MeasureType = 1
  OverTolerance = 0.2
  References2D = -> [ProjItem003]
  Rotation = 0
  ScaleType = 0
  Type = 1
  UnderTolerance = -0.2
  X = -7.39095
  Y = 57.1842
FEATURE [TechDraw::DrawViewDimension] Dimension024
  Arbitrary = false
  FormatSpec = %.2f
  LockPosition = false
  MeasureType = 1
  OverTolerance = 0.2
  References2D = -> [ProjItem003]
  Rotation = 0
  ScaleType = 0
  Type = 2
  UnderTolerance = -0.2
  X = 90.929
  Y = 3.23354
FEATURE [TechDraw::DrawViewAnnotation] Annotation006
  Font = DejaVu Sans
  LineSpace = 80
  LockPosition = false
  MaxWidth = -1
  Rotation = 0
  ScaleType = 0
  Text = Notes: | 1. Material: Al 7075 | 2. Tapping drill \u23001.6 THRU for | screw M2x0.4 | 3. Drill hole \u23004.2 THRU for  | HELICOIL insert M4x0.7x1D | 4. Tapping drill \u23001.6 DEEP 3 | for screw M2x0.4
  TextSize = 6
  TextStyle = 0
  X = 59.9518
  Y = 35.1496
FEATURE [TechDraw::DrawPage] Page002
  KeepUpdated = true
  ProjectionType = 0
  Template = -> Template002
  Views = -> [ProjGroup002,Dimension020,Dimension021,Dimension022,Dimension023,Dimension024,Annotation006]
note: 1 file-system path scrubbed to <path> (originals preserved in the JSON sidecar)
